FCSTD DOCUMENT  (FreeCAD 1.0R39319 (Git))
Label: FrontAssembly
License: All rights reserved
LicenseURL: https://en.wikipedia.org/wiki/All_rights_reserved
objects: App::FeaturePython×19, App::Link×17, Assembly::JointGroup×1, Assembly::AssemblyObject×1
EXTERNAL_REF file=../Parts/FrontCover.FCStd obj=Part
EXTERNAL_REF file=../Parts/WheelLinkage/WheelLinkageTopLeft.FCStd obj=Body
EXTERNAL_REF file=../Parts/WheelLinkage/WheelLinkageBottomLeft.FCStd obj=Part
EXTERNAL_REF file=../Parts/WheelLinkage/WheelLinkageTopRight.FCStd obj=Part
EXTERNAL_REF file=../Parts/WheelLinkage/WheelLinkageBottomRight.FCStd obj=Part
EXTERNAL_REF file=../Parts/FrontWheelAxle/FrontWheelAxleLeft.FCStd obj=Part
EXTERNAL_REF file=../Parts/FrontWheelAxle/FrontWheelAxleRight.FCStd obj=Part
EXTERNAL_REF file=../Parts/S0004m.FCStd obj=Part
EXTERNAL_REF file=../Parts/TBoneLinkage/TBoneLinkageTop.FCStd obj=Part
EXTERNAL_REF file=../Parts/TBoneLinkage/TBoneLinkageBottom.FCStd obj=Part
EXTERNAL_REF file=../Parts/TransferLinkage/TransferLinkageLeft.FCStd obj=Part
EXTERNAL_REF file=../Parts/TransferLinkage/TransferLinkageRight.FCStd obj=Part
EXTERNAL_REF file=../Parts/FrontWheelStopper.FCStd obj=Part
EXTERNAL_REF file=../Parts/Wheel.FCStd obj=Part
EXTERNAL_REF file=../Parts/RpiCamera.FCStd obj=rpiCameraMAssembly

FEATURE [App::Link] FrontCoverPart
  LinkedObject = -> <external ../Parts/FrontCover.FCStd>#Part
FEATURE [App::FeaturePython] GroundedJoint  # Assembly grounded joint (typed FeaturePython)
  ObjectToGround = -> FrontCoverPart
FEATURE [App::Link] WheelLinkageTopLeftBody
  LinkPlacement = pos=(-34,-2e-16,0) rot=(0,0,1;0.017527rad)
  LinkedObject = -> <external ../Parts/WheelLinkage/WheelLinkageTopLeft.FCStd>#Body
  Placement = pos=(-34,-2e-16,0) rot=(0,0,1;0.017527rad)
FEATURE [App::FeaturePython] Joint  label="Revolute"  # Assembly joint (typed FeaturePython)
  Activated = true
  AngleMax = 0
  AngleMin = 0
  Detach1 = false
  Detach2 = false
  Distance = 0
  Distance2 = 0
  EnableAngleMax = false
  EnableAngleMin = false
  EnableLengthMax = false
  EnableLengthMin = false
  JointType = 1 (Revolute)
  LengthMax = 0
  LengthMin = 0
  Placement2 = pos=(-34,-2e-16,0) rot=(0,0,1;0rad)
  Reference1 = -> Assembly [WheelLinkageTopLeftBody.Edge16,WheelLinkageTopLeftBody.Edge16]
  Reference2 = -> Assembly [FrontCoverPart.Body.Edge88,FrontCoverPart.Body.Edge88]
FEATURE [App::Link] WheelLinkageBottomLeftPart
  LinkPlacement = pos=(-34,-2e-16,-7) rot=(0,0,1;0.017527rad)
  LinkedObject = -> <external ../Parts/WheelLinkage/WheelLinkageBottomLeft.FCStd>#Part
  Placement = pos=(-34,-2e-16,-7) rot=(0,0,1;0.017527rad)
FEATURE [App::FeaturePython] Joint001  label="Fixed"  # Assembly joint (typed FeaturePython)
  Activated = true
  AngleMax = 0
  AngleMin = 0
  Detach1 = false
  Detach2 = false
  Distance = 0
  Distance2 = 0
  EnableAngleMax = false
  EnableAngleMin = false
  EnableLengthMax = false
  EnableLengthMin = false
  JointType = 0 (Fixed)
  LengthMax = 0
  LengthMin = 0
  Placement1 = pos=(-5,0,7) rot=(0,0,1;0rad)
  Placement2 = pos=(-5,0,0) rot=(1,0,0;3.14159rad)
  Reference1 = -> Assembly [WheelLinkageBottomLeftPart.Body.Edge27,WheelLinkageBottomLeftPart.Body.Edge27]
  Reference2 = -> Assembly [WheelLinkageTopLeftBody.Edge15,WheelLinkageTopLeftBody.Edge15]
FEATURE [App::Link] WheelLinkageTopRightPart
  LinkPlacement = pos=(34,0,0) rot=(0,0,1;0.017627rad)
  LinkedObject = -> <external ../Parts/WheelLinkage/WheelLinkageTopRight.FCStd>#Part
  Placement = pos=(34,0,0) rot=(0,0,1;0.017627rad)
FEATURE [App::FeaturePython] Joint002  label="Revolute001"  # Assembly joint (typed FeaturePython)
  Activated = true
  AngleMax = 0
  AngleMin = 0
  Detach1 = false
  Detach2 = false
  Distance = 0
  Distance2 = 0
  EnableAngleMax = false
  EnableAngleMin = false
  EnableLengthMax = false
  EnableLengthMin = false
  JointType = 1 (Revolute)
  LengthMax = 0
  LengthMin = 0
  Placement1 = pos=(0,0,0) rot=(0,1,0;3.14159rad)
  Placement2 = pos=(34,0,0) rot=(0,0,1;0rad)
  Reference1 = -> Assembly [WheelLinkageTopRightPart.Part__Mirroring.Edge16,WheelLinkageTopRightPart.Part__Mirroring.Edge16]
  Reference2 = -> Assembly [FrontCoverPart.Body.Edge94,FrontCoverPart.Body.Edge94]
FEATURE [App::Link] WheelLinkageBottomRightPart
  LinkPlacement = pos=(34,0,-7) rot=(0,0,1;0.017627rad)
  LinkedObject = -> <external ../Parts/WheelLinkage/WheelLinkageBottomRight.FCStd>#Part
  Placement = pos=(34,0,-7) rot=(0,0,1;0.017627rad)
FEATURE [App::FeaturePython] Joint003  label="Fixed001"  # Assembly joint (typed FeaturePython)
  Activated = true
  AngleMax = 0
  AngleMin = 0
  Detach1 = false
  Detach2 = false
  Distance = 0
  Distance2 = 0
  EnableAngleMax = false
  EnableAngleMin = false
  EnableLengthMax = false
  EnableLengthMin = false
  JointType = 0 (Fixed)
  LengthMax = 0
  LengthMin = 0
  Placement1 = pos=(5,0,7) rot=(0,1,0;3.14159rad)
  Placement2 = pos=(5,0,0) rot=(0,0,1;3.14159rad)
  Reference1 = -> Assembly [WheelLinkageBottomRightPart.Part__Mirroring.Edge27,WheelLinkageBottomRightPart.Part__Mirroring.Edge27]
  Reference2 = -> Assembly [WheelLinkageTopRightPart.Part__Mirroring.Edge15,WheelLinkageTopRightPart.Part__Mirroring.Edge15]
FEATURE [App::Link] FrontWheelAxleLeftPart
  LinkPlacement = pos=(-31.0005,0.0525794,-3.5) rot=(0,0,1;0.017527rad)
  LinkedObject = -> <external ../Parts/FrontWheelAxle/FrontWheelAxleLeft.FCStd>#Part
  Placement = pos=(-31.0005,0.0525794,-3.5) rot=(0,0,1;0.017527rad)
FEATURE [App::FeaturePython] Joint004  label="Fixed002"  # Assembly joint (typed FeaturePython)
  Activated = true
  AngleMax = 0
  AngleMin = 0
  Detach1 = false
  Detach2 = false
  Distance = 0
  Distance2 = 0
  EnableAngleMax = false
  EnableAngleMin = false
  EnableLengthMax = false
  EnableLengthMin = false
  JointType = 0 (Fixed)
  LengthMax = 0
  LengthMin = 0
  Offset2 = pos=(0,0,0) rot=(0,0,-1;1.5708rad)
  Placement1 = pos=(-3,-2e-16,1.5) rot=(0,0,-1;1.5708rad)
  Placement2 = pos=(0,0,-2) rot=(0,0,-1;1.5708rad)
  Reference1 = -> Assembly [FrontWheelAxleLeftPart.Body.Edge27,FrontWheelAxleLeftPart.Body.Edge27]
  Reference2 = -> Assembly [WheelLinkageTopLeftBody.Edge22,WheelLinkageTopLeftBody.Edge22]
FEATURE [App::Link] FrontWheelAxleRightPart
  LinkPlacement = pos=(31.0005,-0.0528788,-3.5) rot=(0,0,1;0.017627rad)
  LinkedObject = -> <external ../Parts/FrontWheelAxle/FrontWheelAxleRight.FCStd>#Part
  Placement = pos=(31.0005,-0.0528788,-3.5) rot=(0,0,1;0.017627rad)
FEATURE [App::FeaturePython] Joint005  label="Fixed003"  # Assembly joint (typed FeaturePython)
  Activated = true
  AngleMax = 0
  AngleMin = 0
  Detach1 = false
  Detach2 = false
  Distance = 0
  Distance2 = 0
  EnableAngleMax = false
  EnableAngleMin = false
  EnableLengthMax = false
  EnableLengthMin = false
  JointType = 0 (Fixed)
  LengthMax = 0
  LengthMin = 0
  Offset2 = pos=(0,0,0) rot=(0,0,-1;1.5708rad)
  Placement1 = pos=(3,-2e-16,1.5) rot=(-0.707107,0.707107,0;3.14159rad)
  Placement2 = pos=(0,0,-2) rot=(-0.707107,0.707107,0;3.14159rad)
  Reference1 = -> Assembly [FrontWheelAxleRightPart.Part__Mirroring.Edge27,FrontWheelAxleRightPart.Part__Mirroring.Edge27]
  Reference2 = -> Assembly [WheelLinkageTopRightPart.Part__Mirroring.Edge22,WheelLinkageTopRightPart.Part__Mirroring.Edge22]
FEATURE [App::Link] S0004mPart
  LinkPlacement = pos=(0,-9.55,24.5) rot=(1,0,0;3.14159rad)
  LinkedObject = -> <external ../Parts/S0004m.FCStd>#Part
  Placement = pos=(0,-9.55,24.5) rot=(1,0,0;3.14159rad)
FEATURE [App::Link] TBoneLinkageTopPart
  LinkPlacement = pos=(0,-4,1e-16) rot=(0,0,1;0.016716rad)
  LinkedObject = -> <external ../Parts/TBoneLinkage/TBoneLinkageTop.FCStd>#Part
  Placement = pos=(0,-4,1e-16) rot=(0,0,1;0.016716rad)
FEATURE [App::Link] TBoneLinkageBottomPart
  LinkPlacement = pos=(2e-16,-4,-7) rot=(0,0,1;0.016716rad)
  LinkedObject = -> <external ../Parts/TBoneLinkage/TBoneLinkageBottom.FCStd>#Part
  Placement = pos=(2e-16,-4,-7) rot=(0,0,1;0.016716rad)
FEATURE [App::FeaturePython] Joint007  label="Revolute002"  # Assembly joint (typed FeaturePython)
  Activated = true
  AngleMax = 0
  AngleMin = 0
  Detach1 = false
  Detach2 = false
  Distance = 0
  Distance2 = 0
  EnableAngleMax = false
  EnableAngleMin = false
  EnableLengthMax = false
  EnableLengthMin = false
  JointType = 1 (Revolute)
  LengthMax = 0
  LengthMin = 0
  Placement1 = pos=(0,0,-2) rot=(0,0,1;0rad)
  Placement2 = pos=(0,-5.55,26.5) rot=(0,0,1;0rad)
  Reference1 = -> Assembly [TBoneLinkageTopPart.Body.Edge22,TBoneLinkageTopPart.Body.Edge22]
  Reference2 = -> Assembly [S0004mPart.Body.Edge51,S0004mPart.Body.Edge51]
FEATURE [App::FeaturePython] Joint008  label="Fixed005"  # Assembly joint (typed FeaturePython)
  Activated = true
  AngleMax = 0
  AngleMin = 0
  Detach1 = false
  Detach2 = false
  Distance = 0
  Distance2 = 0
  EnableAngleMax = false
  EnableAngleMin = false
  EnableLengthMax = false
  EnableLengthMin = false
  JointType = 0 (Fixed)
  LengthMax = 0
  LengthMin = 0
  Placement1 = pos=(-5,-12,7) rot=(0,0,1;0rad)
  Placement2 = pos=(-5,-12,0) rot=(0,0,1;0rad)
  Reference1 = -> Assembly [TBoneLinkageBottomPart.Body.Edge43,TBoneLinkageBottomPart.Body.Edge43]
  Reference2 = -> Assembly [TBoneLinkageTopPart.Body.Edge16,TBoneLinkageTopPart.Body.Edge16]
FEATURE [App::Link] TransferLinkageLeftPart
  LinkPlacement = pos=(-4.79872,-16.0819,-4.5) rot=(0,0,-1;0.136224rad)
  LinkedObject = -> <external ../Parts/TransferLinkage/TransferLinkageLeft.FCStd>#Part
  Placement = pos=(-4.79872,-16.0819,-4.5) rot=(0,0,-1;0.136224rad)
FEATURE [App::Link] TransferLinkageRightPart
  LinkPlacement = pos=(5.19989,-15.9147,-4.5) rot=(0,0,1;0.133954rad)
  LinkedObject = -> <external ../Parts/TransferLinkage/TransferLinkageRight.FCStd>#Part
  Placement = pos=(5.19989,-15.9147,-4.5) rot=(0,0,1;0.133954rad)
FEATURE [App::FeaturePython] Joint009  label="Revolute003"  # Assembly joint (typed FeaturePython)
  Activated = true
  AngleMax = 0
  AngleMin = 0
  Detach1 = false
  Detach2 = false
  Distance = 0
  Distance2 = 0
  EnableAngleMax = false
  EnableAngleMin = false
  EnableLengthMax = false
  EnableLengthMin = false
  JointType = 1 (Revolute)
  LengthMax = 0
  LengthMin = 0
  Placement1 = pos=(0,0,2) rot=(0,0,1;0rad)
  Placement2 = pos=(-5,-12,-2.5) rot=(1,0,0;3.14159rad)
  Reference1 = -> Assembly [TransferLinkageLeftPart.Body.Edge24,TransferLinkageLeftPart.Body.Edge24]
  Reference2 = -> Assembly [TBoneLinkageTopPart.Body.Edge30,TBoneLinkageTopPart.Body.Edge30]
FEATURE [App::FeaturePython] Joint010  label="Cylindrical"  # Assembly joint (typed FeaturePython)
  Activated = true
  AngleMax = 0
  AngleMin = 0
  Detach1 = false
  Detach2 = false
  Distance = 0
  Distance2 = 0
  EnableAngleMax = false
  EnableAngleMin = false
  EnableLengthMax = false
  EnableLengthMin = false
  JointType = 2 (Cylindrical)
  LengthMax = 0
  LengthMin = 0
  Placement1 = pos=(-32,0,2) rot=(0,0,1;0rad)
  Placement2 = pos=(-2.70757,-11.6906,-2.5) rot=(1,0,0;3.14159rad)
  Reference1 = -> Assembly [TransferLinkageLeftPart.Body.Edge27,TransferLinkageLeftPart.Body.Edge27]
  Reference2 = -> Assembly [WheelLinkageTopLeftBody.Edge26,WheelLinkageTopLeftBody.Edge26]
FEATURE [App::FeaturePython] Joint011  label="Revolute004"  # Assembly joint (typed FeaturePython)
  Activated = true
  AngleMax = 0
  AngleMin = 0
  Detach1 = false
  Detach2 = false
  Distance = 0
  Distance2 = 0
  EnableAngleMax = false
  EnableAngleMin = false
  EnableLengthMax = false
  EnableLengthMin = false
  JointType = 1 (Revolute)
  LengthMax = 0
  LengthMin = 0
  Placement1 = pos=(0,0,2) rot=(0,1,0;3.14159rad)
  Placement2 = pos=(5,-12,-2.5) rot=(1,0,0;3.14159rad)
  Reference1 = -> Assembly [TransferLinkageRightPart.Part__Mirroring.Edge24,TransferLinkageRightPart.Part__Mirroring.Edge24]
  Reference2 = -> Assembly [TBoneLinkageTopPart.Body.Edge31,TBoneLinkageTopPart.Body.Edge31]
FEATURE [App::FeaturePython] Joint012  label="Cylindrical001"  # Assembly joint (typed FeaturePython)
  Activated = true
  AngleMax = 0
  AngleMin = 0
  Detach1 = false
  Detach2 = false
  Distance = 0
  Distance2 = 0
  EnableAngleMax = false
  EnableAngleMin = false
  EnableLengthMax = false
  EnableLengthMin = false
  JointType = 2 (Cylindrical)
  LengthMax = 0
  LengthMin = 0
  Placement1 = pos=(32,0,2) rot=(0,1,0;3.14159rad)
  Placement2 = pos=(2.70757,-11.6906,-2.5) rot=(0,0,1;3.14159rad)
  Reference1 = -> Assembly [TransferLinkageRightPart.Part__Mirroring.Edge27,TransferLinkageRightPart.Part__Mirroring.Edge27]
  Reference2 = -> Assembly [WheelLinkageTopRightPart.Part__Mirroring.Edge26,WheelLinkageTopRightPart.Part__Mirroring.Edge26]
FEATURE [App::Link] FrontWheelStopperPart
  LinkPlacement = pos=(-42.9986,-0.157738,-3.5) rot=(0,0,1;0.017527rad)
  LinkedObject = -> <external ../Parts/FrontWheelStopper.FCStd>#Part
  Placement = pos=(-42.9986,-0.157738,-3.5) rot=(0,0,1;0.017527rad)
FEATURE [App::Link] FrontWheelStopperPart001
  LinkPlacement = pos=(42.9986,0.158636,-3.5) rot=(0,0,1;3.15922rad)
  LinkedObject = -> <external ../Parts/FrontWheelStopper.FCStd>#Part
  Placement = pos=(42.9986,0.158636,-3.5) rot=(0,0,1;3.15922rad)
FEATURE [App::FeaturePython] Joint013  label="Fixed006"  # Assembly joint (typed FeaturePython)
  Activated = true
  AngleMax = 0
  AngleMin = 0
  Detach1 = false
  Detach2 = false
  Distance = 0
  Distance2 = 0
  EnableAngleMax = false
  EnableAngleMin = false
  EnableLengthMax = false
  EnableLengthMin = false
  JointType = 0 (Fixed)
  LengthMax = 0
  LengthMin = 0
  Placement1 = pos=(-2,-2e-16,1.8e-15) rot=(0.57735,0.57735,0.57735;2.0944rad)
  Placement2 = pos=(-14,3e-15,7.1e-15) rot=(0.57735,0.57735,-0.57735;4.18879rad)
  Reference1 = -> Assembly [FrontWheelStopperPart.Body.Edge22,FrontWheelStopperPart.Body.Edge22]
  Reference2 = -> Assembly [FrontWheelAxleLeftPart.Body.Edge20,FrontWheelAxleLeftPart.Body.Edge20]
FEATURE [App::Link] WheelPart
  LinkPlacement = pos=(-35.9997,-0.035053,-3.5) rot=(0,0,1;0.017527rad)
  LinkedObject = -> <external ../Parts/Wheel.FCStd>#Part
  Placement = pos=(-35.9997,-0.035053,-3.5) rot=(0,0,1;0.017527rad)
FEATURE [App::Link] WheelPart001
  LinkPlacement = pos=(35.9997,0.0352525,-3.5) rot=(0,0,1;3.15922rad)
  LinkedObject = -> <external ../Parts/Wheel.FCStd>#Part
  Placement = pos=(35.9997,0.0352525,-3.5) rot=(0,0,1;3.15922rad)
FEATURE [App::FeaturePython] Joint014  label="Fixed007"  # Assembly joint (typed FeaturePython)
  Activated = true
  AngleMax = 0
  AngleMin = 0
  Detach1 = false
  Detach2 = false
  Distance = 0
  Distance2 = 0
  EnableAngleMax = false
  EnableAngleMin = false
  EnableLengthMax = false
  EnableLengthMin = false
  JointType = 0 (Fixed)
  LengthMax = 0
  LengthMin = 0
  Offset2 = pos=(0,0,0) rot=(0,0,1;3.14159rad)
  Placement1 = pos=(-2,-2e-16,1.8e-15) rot=(0.57735,0.57735,0.57735;2.0944rad)
  Placement2 = pos=(14,8.7e-15,3e-16) rot=(-0.57735,0.57735,0.57735;4.18879rad)
  Reference1 = -> Assembly [FrontWheelStopperPart001.Body.Edge22,FrontWheelStopperPart001.Body.Edge22]
  Reference2 = -> Assembly [FrontWheelAxleRightPart.Part__Mirroring.Edge6,FrontWheelAxleRightPart.Part__Mirroring.Edge6]
FEATURE [App::FeaturePython] Joint015  label="Fixed008"  # Assembly joint (typed FeaturePython)
  Activated = true
  AngleMax = 0
  AngleMin = 0
  Detach1 = false
  Detach2 = false
  Distance = 0
  Distance2 = 0
  EnableAngleMax = false
  EnableAngleMin = false
  EnableLengthMax = false
  EnableLengthMin = false
  JointType = 0 (Fixed)
  LengthMax = 0
  LengthMin = 0
  Placement1 = pos=(-11,7.8e-15,-3.9e-15) rot=(0.57735,0.57735,0.57735;2.0944rad)
  Placement2 = pos=(-16,4e-15,7.1e-15) rot=(0.57735,0.57735,-0.57735;4.18879rad)
  Reference1 = -> Assembly [WheelPart.Body.Edge25,WheelPart.Body.Edge25]
  Reference2 = -> Assembly [FrontWheelAxleLeftPart.Body.Edge33,FrontWheelAxleLeftPart.Body.Edge33]
FEATURE [App::FeaturePython] Joint016  label="Fixed009"  # Assembly joint (typed FeaturePython)
  Activated = true
  AngleMax = 0
  AngleMin = 0
  Detach1 = false
  Detach2 = false
  Distance = 0
  Distance2 = 0
  EnableAngleMax = false
  EnableAngleMin = false
  EnableLengthMax = false
  EnableLengthMin = false
  JointType = 0 (Fixed)
  LengthMax = 0
  LengthMin = 0
  Offset2 = pos=(0,0,0) rot=(0,0,1;3.14159rad)
  Placement1 = pos=(-11,7.8e-15,-3.9e-15) rot=(0.57735,0.57735,0.57735;2.0944rad)
  Placement2 = pos=(16,4e-15,7.1e-15) rot=(-0.57735,0.57735,0.57735;4.18879rad)
  Reference1 = -> Assembly [WheelPart001.Body.Edge25,WheelPart001.Body.Edge25]
  Reference2 = -> Assembly [FrontWheelAxleRightPart.Part__Mirroring.Edge33,FrontWheelAxleRightPart.Part__Mirroring.Edge33]
FEATURE [App::Link] RpiCameraPart
  LinkPlacement = pos=(-3.5e-15,11.25,15.75) rot=(0,0,1;0rad)
  LinkedObject = -> <external ../Parts/RpiCamera.FCStd>#rpiCameraMAssembly
  Placement = pos=(-3.5e-15,11.25,15.75) rot=(0,0,1;0rad)
FEATURE [App::FeaturePython] Joint017  label="Fixed010"  # Assembly joint (typed FeaturePython)
  Activated = true
  AngleMax = 0
  AngleMin = 0
  Detach1 = false
  Detach2 = false
  Distance = 0
  Distance2 = 0
  EnableAngleMax = false
  EnableAngleMin = false
  EnableLengthMax = false
  EnableLengthMin = false
  JointType = 0 (Fixed)
  LengthMax = 0
  LengthMin = 0
  Offset2 = pos=(0,0,1.7) rot=(0,0,-1;1.5708rad)
  Placement1 = pos=(10.25,0.1,3.75) rot=(-0.57735,0.57735,0.57735;2.0944rad)
  Placement2 = pos=(10.25,11.35,19.5) rot=(-0.57735,0.57735,0.57735;2.0944rad)
  Reference1 = -> Assembly [RpiCameraPart.Part__Feature.Edge767,RpiCameraPart.Part__Feature.Edge767]
  Reference2 = -> Assembly [FrontCoverPart.Body.Edge102,FrontCoverPart.Body.Edge102]
FEATURE [App::FeaturePython] Joint018  label="Fixed011"  # Assembly joint (typed FeaturePython)
  Activated = true
  AngleMax = 0
  AngleMin = 0
  Detach1 = false
  Detach2 = false
  Distance = 0
  Distance2 = 0
  EnableAngleMax = false
  EnableAngleMin = false
  EnableLengthMax = false
  EnableLengthMin = false
  JointType = 0 (Fixed)
  LengthMax = 0
  LengthMin = 0
  Placement1 = pos=(0,-21.35,8.5) rot=(0,0,1;0rad)
  Placement2 = pos=(0,11.8,16) rot=(0,0,1;0rad)
  Reference1 = -> Assembly [FrontCoverPart.Body.Edge133,FrontCoverPart.Body.Edge133]
  Reference2 = -> Assembly [S0004mPart.Body.Edge42,S0004mPart.Body.Edge42]
FEATURE [Assembly::JointGroup] Joints
  Group = -> [GroundedJoint,Joint,Joint001,Joint002,Joint003,Joint004,Joint005,Joint007,Joint008,Joint009,Joint010,Joint011,Joint012,Joint013,Joint014,Joint015,Joint016,Joint017,Joint018]
FEATURE [Assembly::AssemblyObject] Assembly  label="FrontAssembly"
  Group = -> [Joints,FrontCoverPart,GroundedJoint,WheelLinkageTopLeftBody,Joint,WheelLinkageBottomLeftPart,Joint001,WheelLinkageTopRightPart,Joint002,WheelLinkageBottomRightPart,Joint003,FrontWheelAxleLeftPart,Joint004,FrontWheelAxleRightPart,Joint005,S0004mPart,TBoneLinkageTopPart,TBoneLinkageBottomPart,Joint007,Joint008,TransferLinkageLeftPart,TransferLinkageRightPart,Joint009,Joint010,Joint011,Joint012,+11 more]
  Origin = -> Origin
  Type = Assembly

RESOLVED EXTERNAL PARTS (link-assembly join: the EXTERNAL_REF files above that resolve inside this repo's crawl, each included once):
---- part ../Parts/FrontCover.FCStd = doc fcstd_34d13ded4ae3 ----
FCSTD DOCUMENT  (FreeCAD 1.0R39319 (Git))
Label: FrontCover
License: All rights reserved
LicenseURL: https://en.wikipedia.org/wiki/All_rights_reserved
objects: Sketcher::SketchObject×5, PartDesign::Pad×3, PartDesign::SubShapeBinder×2, PartDesign::Pocket×2, PartDesign::Chamfer×1, PartDesign::Body×1, App::Part×1
note: 31 computed .brp shape members not serialized (recipe doc carries the construction recipe); baked Part::Feature solids carry a one-line shape summary decoded from their .brp
EXTERNAL_REF file=../Models/SteeringAckermannModel.FCStd obj=Part
EXTERNAL_REF file=Chassis.FCStd obj=Part

FEATURE [PartDesign::SubShapeBinder] Binder  label="SteeringAckermannModel"
  BindCopyOnChange = 0
  BindMode = 0
  ClaimChildren = false
  Context = -> Part [Body.Binder.]
  Fuse = false
  MakeFace = true
  OffsetFill = false
  OffsetIntersection = false
  OffsetJoinType = 0
  OffsetOpenResult = false
  PartialLoad = false
  Refine = true
  Relative = true
  Support = -> [<external ../Models/SteeringAckermannModel.FCStd>#Part[Sketch001.]]
  _Version = 2
FEATURE [PartDesign::SubShapeBinder] Binder001  label="ChassisSketch002"
  BindCopyOnChange = 0
  BindMode = 0
  ClaimChildren = false
  Context = -> Part [Body.Binder001.]
  Fuse = false
  MakeFace = true
  OffsetFill = false
  OffsetIntersection = false
  OffsetJoinType = 0
  OffsetOpenResult = false
  PartialLoad = false
  Refine = true
  Relative = true
  Support = -> [<external Chassis.FCStd>#Part[Body.Sketch002.]]
  _Version = 2
FEATURE [Sketcher::SketchObject] Sketch
  ArcFitTolerance = 1e-06
  AttachmentSupport = -> [XY_Plane001]
  ExternalGeometry = -> [Binder001,Binder]
  FullyConstrained = true
  MakeInternals = false
  MapMode = 5
  sketch-geometry (27):
    g0: LineSegment StartX=-11.3 StartY=-4 StartZ=0 EndX=-26 EndY=-4 EndZ=0
    g1: LineSegment StartX=-26 StartY=-4 StartZ=0 EndX=-34 EndY=-4 EndZ=0
    g2: LineSegment StartX=-34 StartY=4 StartZ=0 EndX=-26 EndY=4 EndZ=0
    g3: LineSegment StartX=-26 StartY=4 StartZ=0 EndX=-10 EndY=22 EndZ=0
    g4: ArcOfCircle CenterX=-34 CenterY=-2e-16 CenterZ=0 NormalX=0 NormalY=0 NormalZ=1 AngleXU=0 Radius=4 StartAngle=1.5708 EndAngle=4.71239
    g5: LineSegment StartX=11.3 StartY=-4 StartZ=0 EndX=26 EndY=-4 EndZ=0
    g6: LineSegment StartX=26 StartY=4 StartZ=0 EndX=10 EndY=22 EndZ=0
    g7: LineSegment StartX=26 StartY=-4 StartZ=0 EndX=34 EndY=-4 EndZ=0
    g8: LineSegment StartX=26 StartY=4 StartZ=0 EndX=34 EndY=4 EndZ=0
    g9: ArcOfCircle CenterX=34 CenterY=0 CenterZ=0 NormalX=0 NormalY=0 NormalZ=1 AngleXU=0 Radius=4 StartAngle=4.71239 EndAngle=7.85398
    g10: LineSegment StartX=-10 StartY=22 StartZ=0 EndX=10 EndY=22 EndZ=0
    g11: LineSegment StartX=-11.3 StartY=-4 StartZ=0 EndX=-6 EndY=-23.75 EndZ=0
    g12: LineSegment StartX=-6 StartY=-23.75 StartZ=0 EndX=6 EndY=-23.75 EndZ=0
    g13: LineSegment StartX=6 StartY=-23.75 StartZ=0 EndX=11.3 EndY=-4 EndZ=0
    g14: LineSegment StartX=-4.35 StartY=0.65 StartZ=0 EndX=-4.35 EndY=-19.75 EndZ=0
    g15: LineSegment StartX=-4.35 StartY=-19.75 StartZ=0 EndX=4.35 EndY=-19.75 EndZ=0
    g16: LineSegment StartX=4.35 StartY=-19.75 StartZ=0 EndX=4.35 EndY=0.65 EndZ=0
    g17: LineSegment StartX=4.35 StartY=0.65 StartZ=0 EndX=-4.35 EndY=0.65 EndZ=0
    g18: GeomPoint X=4e-16 Y=-9.55 Z=0
    g19: Circle CenterX=0 CenterY=2.25 CenterZ=0 NormalX=0 NormalY=0 NormalZ=1 AngleXU=0 Radius=0.86
    g20: Circle CenterX=-7.473e-13 CenterY=-21.35 CenterZ=0 NormalX=0 NormalY=0 NormalZ=1 AngleXU=0 Radius=0.86
    g21: Circle CenterX=-34 CenterY=-2e-16 CenterZ=0 NormalX=0 NormalY=0 NormalZ=1 AngleXU=0 Radius=1.5
    g22: Circle CenterX=34 CenterY=0 CenterZ=0 NormalX=0 NormalY=0 NormalZ=1 AngleXU=0 Radius=1.5
    g23: Circle CenterX=-22 CenterY=0 CenterZ=0 NormalX=0 NormalY=0 NormalZ=1 AngleXU=0 Radius=1.65
    g24: Circle CenterX=-11.3195 CenterY=16 CenterZ=0 NormalX=0 NormalY=0 NormalZ=1 AngleXU=0 Radius=1.65
    g25: Circle CenterX=11.3195 CenterY=16 CenterZ=0 NormalX=0 NormalY=0 NormalZ=1 AngleXU=0 Radius=1.65
    g26: Circle CenterX=22 CenterY=0 CenterZ=0 NormalX=0 NormalY=0 NormalZ=1 AngleXU=0 Radius=1.65
  constraints (58):
    c: Coincident(g0,g-3)
    c: Coincident(g0,g-4)
    c: Coincident(g1,g0)
    c: Coincident(g2,g-7)
    c: Coincident(g3,g2)
    c: Coincident(g3,g-8)
    c: Tangent(g1,g4) = 1.5708
    c: Tangent(g2,g4) = 1.5708
    c: Coincident(g1,g-5)
    c: Horizontal(g2)
    c: Coincident(g5,g-12)
    c: Coincident(g5,g-13)
    c: Coincident(g6,g-16)
    c: Coincident(g6,g-17)
    c: Coincident(g7,g5)
    c: Coincident(g8,g6)
    c: Tangent(g7,g9) = -1.5708
    c: Tangent(g9,g8) = 1.5708
    c: Horizontal(g8)
    c: Coincident(g7,g-14)
    c: Coincident(g10,g3)
    c: Coincident(g10,g6)
    c: Coincident(g11,g0)
    c: Coincident(g12,g11)
    c: Coincident(g13,g12)
    c: Coincident(g13,g5)
    c: Symmetric(g11,g12,g-2)
    c: DistanceX(g12,g12) = 12
    c: Coincident(g14,g15)
    c: Coincident(g15,g16)
    c: Coincident(g16,g17)
    c: Coincident(g17,g14)
    c: Vertical(g14)
    c: Vertical(g16)
    c: Horizontal(g17)
    c: Symmetric(g14,g15,g-2)
    c: DistanceX(g15,g15) = 8.7
    c: DistanceY(g14,g14) = 20.4
    c: Distance(g-21,g17) = 4.65
    c: Distance(g12,g15) = 4
    c: Symmetric(g14,g16,g18)
    c: Diameter(g19) = 1.72
    c: PointOnObject(g19,g-2)
    c: Equal(g19,g20)
    c: Symmetric(g19,g20,g18)
    c: Distance(g19,g17) = 1.6
    c: Coincident(g21,g4)
    c: Equal(g21,g-9)
    c: Coincident(g22,g9)
    c: Equal(g22,g-18)
    c: Coincident(g23,g-10)
    c: Coincident(g24,g-11)
    c: Coincident(g25,g-20)
    c: Coincident(g26,g-19)
    c: Equal(g23,g26)
    c: Equal(g24,g25)
    c: Diameter(g23) = 3.3
    c: Diameter(g24) = 3.3
FEATURE [PartDesign::Pad] Pad
  Direction = (0,0,1)
  Length = 3
  Length2 = 10
  Profile = -> Sketch
  ReferenceAxis = -> Sketch [N_Axis]
  Refine = true
  Suppressed = false
  Type = 0
FEATURE [Sketcher::SketchObject] Sketch001
  ArcFitTolerance = 1e-06
  AttachmentSupport = -> [Pad]
  ExternalGeometry = -> [Sketch]
  FullyConstrained = true
  MakeInternals = false
  MapMode = 5
  Placement = pos=(0,0,3) rot=(0,0,1;0rad)
  sketch-geometry (13):
    g0: LineSegment StartX=-4.35 StartY=-19.75 StartZ=0 EndX=4.35 EndY=-19.75 EndZ=0
    g1: LineSegment StartX=4.35 StartY=-19.75 StartZ=0 EndX=4.35 EndY=0.65 EndZ=0
    g2: LineSegment StartX=4.35 StartY=0.65 StartZ=0 EndX=-4.35 EndY=0.65 EndZ=0
    g3: LineSegment StartX=-4.35 StartY=0.65 StartZ=0 EndX=-4.35 EndY=-19.75 EndZ=0
    g4: Circle CenterX=0 CenterY=-21.35 CenterZ=0 NormalX=0 NormalY=0 NormalZ=1 AngleXU=0 Radius=0.86
    g5: Circle CenterX=0 CenterY=2.25 CenterZ=0 NormalX=0 NormalY=0 NormalZ=1 AngleXU=0 Radius=0.86
    g6: LineSegment StartX=-6 StartY=-23.75 StartZ=0 EndX=6 EndY=-23.75 EndZ=0
    g7: LineSegment [constr] StartX=-9.81063 StartY=-9.55 StartZ=0 EndX=9.81063 EndY=-9.55 EndZ=0
    g8: LineSegment StartX=-6 StartY=-23.75 StartZ=0 EndX=-9.81063 EndY=-9.55 EndZ=0
    g9: LineSegment StartX=6 StartY=-23.75 StartZ=0 EndX=9.81063 EndY=-9.55 EndZ=0
    g10: LineSegment StartX=-6 StartY=4.65 StartZ=0 EndX=-9.81063 EndY=-9.55 EndZ=0
    g11: LineSegment StartX=-6 StartY=4.65 StartZ=0 EndX=6 EndY=4.65 EndZ=0
    g12: LineSegment StartX=6 StartY=4.65 StartZ=0 EndX=9.81063 EndY=-9.55 EndZ=0
  constraints (27):
    c: Coincident(g0,g-10)
    c: Coincident(g0,g-11)
    c: Coincident(g1,g0)
    c: Coincident(g1,g-12)
    c: Coincident(g2,g1)
    c: Coincident(g2,g-12)
    c: Coincident(g3,g2)
    c: Coincident(g3,g0)
    c: Coincident(g4,g-7)
    c: Equal(g4,g-7)
    c: Coincident(g5,g-8)
    c: Equal(g5,g-8)
    c: Coincident(g6,g-5)
    c: Coincident(g6,g-6)
    c: Horizontal(g7)
    c: Symmetric(g7,g7,g-3)
    c: PointOnObject(g7,g-4)
    c: Coincident(g8,g6)
    c: Coincident(g8,g7)
    c: Coincident(g9,g6)
    c: Coincident(g9,g7)
    c: Coincident(g10,g11)
    c: Coincident(g12,g11)
    c: Symmetric(g6,g10,g7)
    c: Symmetric(g6,g11,g7)
    c: Coincident(g10,g7)
    c: Coincident(g12,g7)
FEATURE [PartDesign::Pad] Pad001
  BaseFeature = -> Pad
  Direction = (0,0,1)
  Length = 5.5
  Length2 = 10
  Profile = -> Sketch001
  ReferenceAxis = -> Sketch001 [N_Axis]
  Refine = true
  Suppressed = false
  Type = 0
FEATURE [Sketcher::SketchObject] Sketch002
  ArcFitTolerance = 1e-06
  AttachmentSupport = -> [Pad001]
  ExternalGeometry = -> [Sketch001]
  FullyConstrained = true
  MakeInternals = false
  MapMode = 5
  Placement = pos=(0,0,3) rot=(0,0,1;0rad)
  sketch-geometry (8):
    g0: LineSegment StartX=-12 StartY=6.65 StartZ=0 EndX=-12 EndY=-1.35 EndZ=0
    g1: LineSegment StartX=-12 StartY=-1.35 StartZ=0 EndX=-13.5 EndY=-1.35 EndZ=0
    g2: LineSegment StartX=-13.5 StartY=-1.35 StartZ=0 EndX=-13.5 EndY=9.65 EndZ=0
    g3: LineSegment StartX=-12 StartY=6.65 StartZ=0 EndX=12 EndY=6.65 EndZ=0
    g4: LineSegment StartX=-13.5 StartY=9.65 StartZ=0 EndX=13.5 EndY=9.65 EndZ=0
    g5: LineSegment StartX=12 StartY=6.65 StartZ=0 EndX=12 EndY=-1.35 EndZ=0
    g6: LineSegment StartX=12 StartY=-1.35 StartZ=0 EndX=13.5 EndY=-1.35 EndZ=0
    g7: LineSegment StartX=13.5 StartY=-1.35 StartZ=0 EndX=13.5 EndY=9.65 EndZ=0
  constraints (20):
    c: Vertical(g0)
    c: Coincident(g1,g0)
    c: Horizontal(g1)
    c: Coincident(g2,g1)
    c: Vertical(g2)
    c: Coincident(g3,g0)
    c: Coincident(g4,g2)
    c: Symmetric(g2,g4,g-2)
    c: Symmetric(g0,g3,g-2)
    c: Coincident(g5,g3)
    c: Coincident(g6,g5)
    c: Coincident(g7,g6)
    c: Coincident(g7,g4)
    c: Symmetric(g1,g6,g-2)
    c: Symmetric(g0,g5,g-2)
    c: DistanceX(g1,g1) = 1.5
    c: DistanceY(g0,g0) = 8
    c: Distance(g4,g3) = 3
    c: Distance(g-3,g3) = 2
    c: DistanceX(g4,g4) = 27
FEATURE [PartDesign::Pad] Pad002
  BaseFeature = -> Pad001
  Direction = (0,0,1)
  Length = 36
  Length2 = 10
  Profile = -> Sketch002
  ReferenceAxis = -> Sketch002 [N_Axis]
  Refine = true
  Suppressed = false
  Type = 0
FEATURE [PartDesign::Chamfer] Chamfer
  Angle = 15
  Base = -> Pad002 [Edge107,Edge99]
  BaseFeature = -> Pad002
  ChamferType = 2
  FlipDirection = false
  Refine = true
  Size = 29.85
  Size2 = 1
  SupportTransform = false
  Suppressed = false
  UseAllEdges = false
FEATURE [Sketcher::SketchObject] Sketch003
  ArcFitTolerance = 1e-06
  AttachmentSupport = -> [Chamfer]
  ExternalGeometry = -> [Chamfer]
  FullyConstrained = true
  MakeInternals = false
  MapMode = 5
  Placement = pos=(0,9.65,0) rot=(0,0.707107,0.707107;3.14159rad)
  sketch-geometry (14):
    g0: LineSegment [constr] StartX=-10.25 StartY=6 StartZ=0 EndX=10.25 EndY=6 EndZ=0
    g1: LineSegment [constr] StartX=10.25 StartY=6 StartZ=0 EndX=10.25 EndY=19.5 EndZ=0
    g2: LineSegment [constr] StartX=10.25 StartY=19.5 StartZ=0 EndX=-10.25 EndY=19.5 EndZ=0
    g3: LineSegment [constr] StartX=-10.25 StartY=19.5 StartZ=0 EndX=-10.25 EndY=6 EndZ=0
    g4: GeomPoint [constr] X=0 Y=12.75 Z=0
    g5: Circle CenterX=-10.25 CenterY=6 CenterZ=0 NormalX=0 NormalY=0 NormalZ=1 AngleXU=0 Radius=1.05
    g6: Circle CenterX=-10.25 CenterY=19.5 CenterZ=0 NormalX=0 NormalY=0 NormalZ=1 AngleXU=0 Radius=1.05
    g7: Circle CenterX=10.25 CenterY=6 CenterZ=0 NormalX=0 NormalY=0 NormalZ=1 AngleXU=0 Radius=1.05
    g8: Circle CenterX=10.25 CenterY=19.5 CenterZ=0 NormalX=0 NormalY=0 NormalZ=1 AngleXU=0 Radius=1.05
    g9: LineSegment StartX=-10 StartY=33.5 StartZ=0 EndX=10 EndY=33.5 EndZ=0
    g10: LineSegment StartX=10 StartY=33.5 StartZ=0 EndX=10 EndY=36.5 EndZ=0
    g11: LineSegment StartX=10 StartY=36.5 StartZ=0 EndX=-10 EndY=36.5 EndZ=0
    g12: LineSegment StartX=-10 StartY=36.5 StartZ=0 EndX=-10 EndY=33.5 EndZ=0
    g13: GeomPoint [constr] X=0 Y=35 Z=0
  constraints (34):
    c: Coincident(g0,g1)
    c: Coincident(g1,g2)
    c: Coincident(g2,g3)
    c: Coincident(g3,g0)
    c: Horizontal(g0)
    c: Horizontal(g2)
    c: Vertical(g1)
    c: Vertical(g3)
    c: Symmetric(g2,g0,g4)
    c: PointOnObject(g4,g-2)
    c: Diameter(g5) = 2.1
    c: Coincident(g6,g2)
    c: Coincident(g7,g0)
    c: Coincident(g8,g1)
    c: Equal(g5,g6)
    c: Equal(g5,g7)
    c: Equal(g6,g8)
    c: DistanceX(g0,g0) = 20.5
    c: DistanceY(g3,g3) = 13.5
    c: Distance(g0,g-3) = 3
    c: Coincident(g5,g0)
    c: Coincident(g9,g10)
    c: Coincident(g10,g11)
    c: Coincident(g11,g12)
    c: Coincident(g12,g9)
    c: Horizontal(g9)
    c: Horizontal(g11)
    c: Vertical(g10)
    c: Vertical(g12)
    c: Symmetric(g11,g9,g13)
    c: PointOnObject(g13,g-2)
    c: DistanceX(g9,g9) = 20
    c: DistanceY(g12,g12) = 3
    c: DistanceY(g2,g9) = 14
FEATURE [PartDesign::Pocket] Pocket
  BaseFeature = -> Chamfer
  Direction = (0,-1,2e-16)
  Length = 0
  Length2 = 5
  Profile = -> Sketch003
  ReferenceAxis = -> Sketch003 [N_Axis]
  Refine = true
  Suppressed = false
  Type = 3
  UpToFace = -> Chamfer [Face6]
FEATURE [Sketcher::SketchObject] Sketch004
  ArcFitTolerance = 1e-06
  AttachmentSupport = -> [Pocket]
  ExternalGeometry = -> [Binder001,Sketch,Sketch001]
  FullyConstrained = true
  MakeInternals = false
  MapMode = 5
  Placement = pos=(0,0,0) rot=(1,0,0;3.14159rad)
  sketch-geometry (8):
    g0: LineSegment StartX=-8 StartY=2.75 StartZ=0 EndX=-11.3 EndY=4 EndZ=0
    g1: LineSegment StartX=-11.3 StartY=4 StartZ=0 EndX=-6 EndY=23.75 EndZ=0
    g2: LineSegment StartX=-6 StartY=23.75 StartZ=0 EndX=6 EndY=23.75 EndZ=0
    g3: LineSegment StartX=6 StartY=23.75 StartZ=0 EndX=11.3 EndY=4 EndZ=0
    g4: LineSegment StartX=11.3 StartY=4 StartZ=0 EndX=8 EndY=2.75 EndZ=0
    g5: LineSegment StartX=-8 StartY=2.75 StartZ=0 EndX=-6 EndY=-4.65 EndZ=0
    g6: LineSegment StartX=-6 StartY=-4.65 StartZ=0 EndX=6 EndY=-4.65 EndZ=0
    g7: LineSegment StartX=6 StartY=-4.65 StartZ=0 EndX=8 EndY=2.75 EndZ=0
  constraints (16):
    c: Coincident(g0,g-7)
    c: Coincident(g1,g0)
    c: Coincident(g1,g-8)
    c: Coincident(g2,g1)
    c: Coincident(g2,g-9)
    c: Coincident(g3,g2)
    c: Coincident(g3,g-9)
    c: Coincident(g4,g3)
    c: Coincident(g4,g-6)
    c: Coincident(g0,g-4)
    c: Coincident(g5,g0)
    c: Coincident(g5,g-11)
    c: Coincident(g6,g5)
    c: Coincident(g6,g-12)
    c: Coincident(g7,g6)
    c: Coincident(g7,g4)
FEATURE [PartDesign::Pocket] Pocket001
  BaseFeature = -> Pocket
  Direction = (0,0,1)
  Length = 1
  Length2 = 5
  Profile = -> Sketch004
  ReferenceAxis = -> Sketch004 [N_Axis]
  Refine = true
  Suppressed = false
  Type = 0
FEATURE [PartDesign::Body] Body  label="FrontCoverBody"
  AllowCompound = false
  Group = -> [Binder,Binder001,Sketch,Pad,Sketch001,Pad001,Sketch002,Pad002,Chamfer,Sketch003,Pocket,Sketch004,Pocket001]
  Origin = -> Origin001
  Tip = -> Pocket001
FEATURE [App::Part] Part  label="FrontCoverPart"
  Group = -> [Body]
  Origin = -> Origin
---- part ../Parts/FrontWheelAxle/FrontWheelAxleLeft.FCStd = doc fcstd_68c86e5070d7 ----
FCSTD DOCUMENT  (FreeCAD 1.0R39285 (Git))
Label: FrontWheelAxleLeft
License: All rights reserved
LicenseURL: https://en.wikipedia.org/wiki/All_rights_reserved
objects: Sketcher::SketchObject×5, PartDesign::Pad×4, PartDesign::Chamfer×3, PartDesign::Pocket×1, PartDesign::Body×1, App::Part×1
note: 35 computed .brp shape members not serialized (recipe doc carries the construction recipe); baked Part::Feature solids carry a one-line shape summary decoded from their .brp

FEATURE [Sketcher::SketchObject] Sketch
  ArcFitTolerance = 1e-06
  AttachmentSupport = -> [YZ_Plane001]
  FullyConstrained = true
  MakeInternals = false
  MapMode = 5
  Placement = pos=(0,0,0) rot=(0.57735,0.57735,0.57735;2.0944rad)
  sketch-geometry (4):
    g0: ArcOfCircle CenterX=0 CenterY=0 CenterZ=0 NormalX=0 NormalY=0 NormalZ=1 AngleXU=0 Radius=4.525 StartAngle=2.80371 EndAngle=3.47948
    g1: ArcOfCircle CenterX=0 CenterY=0 CenterZ=0 NormalX=0 NormalY=0 NormalZ=1 AngleXU=0 Radius=4.525 StartAngle=5.9453 EndAngle=6.62107
    g2: LineSegment StartX=-4.26915 StartY=1.5 StartZ=0 EndX=4.26915 EndY=1.5 EndZ=0
    g3: LineSegment StartX=4.26915 StartY=-1.5 StartZ=0 EndX=-4.26915 EndY=-1.5 EndZ=0
  constraints (12):
    c: Coincident(g0,g-1)
    c: Coincident(g1,g0)
    c: Coincident(g2,g0)
    c: Coincident(g2,g1)
    c: Horizontal(g2)
    c: Coincident(g3,g1)
    c: Coincident(g3,g0)
    c: Horizontal(g3)
    c: Equal(g0,g1)
    c: Equal(g3,g2)
    c: Diameter(g0) = 9.05
    c: Distance(g2,g3) = 3
FEATURE [PartDesign::Pad] Pad
  Direction = (1,0,0)
  Length = 11
  Length2 = 10
  Placement = pos=(0,0,0) rot=(1,1,1;2.0944rad)
  Profile = -> Sketch
  ReferenceAxis = -> Sketch [N_Axis]
  Refine = true
  Reversed = true
  Suppressed = false
  Type = 0
FEATURE [Sketcher::SketchObject] Sketch001
  ArcFitTolerance = 1e-06
  AttachmentSupport = -> [Pad]
  ExternalGeometry = -> [Sketch]
  FullyConstrained = true
  MakeInternals = false
  MapMode = 5
  Placement = pos=(-11,0,0) rot=(0.57735,0.57735,-0.57735;4.18879rad)
  sketch-geometry (1):
    g0: Circle CenterX=0 CenterY=0 CenterZ=0 NormalX=0 NormalY=0 NormalZ=1 AngleXU=0 Radius=4.525
  constraints (2):
    c: Coincident(g0,g-1)
    c: Equal(g0,g-3)
FEATURE [PartDesign::Pad] Pad001
  BaseFeature = -> Pad
  Direction = (-1,0,0)
  Length = 3
  Length2 = 10
  Placement = pos=(0,0,0) rot=(1,1,1;2.0944rad)
  Profile = -> Sketch001
  ReferenceAxis = -> Sketch001 [N_Axis]
  Refine = true
  Suppressed = false
  Type = 0
FEATURE [Sketcher::SketchObject] Sketch002
  ArcFitTolerance = 1e-06
  AttachmentSupport = -> [Pad001]
  FullyConstrained = true
  MakeInternals = false
  MapMode = 5
  Placement = pos=(-14,0,0) rot=(0.57735,0.57735,-0.57735;4.18879rad)
  sketch-geometry (1):
    g0: Circle CenterX=0 CenterY=0 CenterZ=0 NormalX=0 NormalY=0 NormalZ=1 AngleXU=0 Radius=6.5
  constraints (2):
    c: Coincident(g0,g-1)
    c: Diameter(g0) = 13
FEATURE [PartDesign::Pad] Pad002
  BaseFeature = -> Pad001
  Direction = (-1,0,0)
  Length = 2
  Length2 = 10
  Placement = pos=(0,0,0) rot=(1,1,1;2.0944rad)
  Profile = -> Sketch002
  ReferenceAxis = -> Sketch002 [N_Axis]
  Refine = true
  Suppressed = false
  Type = 0
FEATURE [Sketcher::SketchObject] Sketch003
  ArcFitTolerance = 1e-06
  AttachmentSupport = -> [Pad002]
  ExternalGeometry = -> [Sketch]
  FullyConstrained = true
  MakeInternals = false
  MapMode = 5
  Placement = pos=(-16,0,0) rot=(0.57735,0.57735,-0.57735;4.18879rad)
  sketch-geometry (1):
    g0: Circle CenterX=0 CenterY=0 CenterZ=0 NormalX=0 NormalY=0 NormalZ=1 AngleXU=0 Radius=4.525
  constraints (2):
    c: Coincident(g0,g-1)
    c: Equal(g0,g-3)
FEATURE [PartDesign::Pad] Pad003
  BaseFeature = -> Pad002
  Direction = (-1,0,0)
  Length = 10
  Length2 = 10
  Placement = pos=(0,0,0) rot=(1,1,1;2.0944rad)
  Profile = -> Sketch003
  ReferenceAxis = -> Sketch003 [N_Axis]
  Refine = true
  Suppressed = false
  Type = 0
FEATURE [Sketcher::SketchObject] Sketch004
  ArcFitTolerance = 1e-06
  AttachmentSupport = -> [Pad003]
  FullyConstrained = true
  MakeInternals = false
  MapMode = 5
  Placement = pos=(0,3e-16,1.5) rot=(0,0,-1;1.5708rad)
  sketch-geometry (2):
    g0: Circle CenterX=0 CenterY=-3 CenterZ=0 NormalX=0 NormalY=0 NormalZ=1 AngleXU=0 Radius=1.62
    g1: Circle CenterX=0 CenterY=-8 CenterZ=0 NormalX=0 NormalY=0 NormalZ=1 AngleXU=0 Radius=1.68
  constraints (6):
    c: Diameter(g0) = 3.24
    c: PointOnObject(g0,g-2)
    c: DistanceY(g0,g-1) = 3
    c: Diameter(g1) = 3.36
    c: PointOnObject(g1,g-2)
    c: DistanceY(g1,g0) = 5
FEATURE [PartDesign::Pocket] Pocket
  BaseFeature = -> Pad003
  Direction = (0,0,-1)
  Length = 0
  Length2 = 5
  Placement = pos=(0,0,0) rot=(1,1,1;2.0944rad)
  Profile = -> Sketch004
  ReferenceAxis = -> Sketch004 [N_Axis]
  Refine = true
  Suppressed = false
  Type = 3
  UpToFace = -> Pad003 [Face5]
FEATURE [PartDesign::Chamfer] Chamfer
  Angle = 45
  Base = -> Pocket [Edge27]
  BaseFeature = -> Pocket
  ChamferType = 1
  FlipDirection = false
  Placement = pos=(0,0,0) rot=(1,1,1;2.0944rad)
  Refine = true
  Size = 2
  Size2 = 1
  SupportTransform = false
  Suppressed = false
  UseAllEdges = false
FEATURE [PartDesign::Chamfer] Chamfer001
  Angle = 45
  Base = -> Chamfer [Edge10]
  BaseFeature = -> Chamfer
  ChamferType = 1
  FlipDirection = false
  Placement = pos=(0,0,0) rot=(1,1,1;2.0944rad)
  Refine = true
  Size = 9
  Size2 = 2.2
  SupportTransform = false
  Suppressed = false
  UseAllEdges = false
FEATURE [PartDesign::Chamfer] Chamfer002
  Angle = 45
  Base = -> Chamfer001 [Edge10,Edge7]
  BaseFeature = -> Chamfer001
  ChamferType = 1
  FlipDirection = false
  Placement = pos=(0,0,0) rot=(1,1,1;2.0944rad)
  Refine = true
  Size = 3
  Size2 = 2
  SupportTransform = false
  Suppressed = false
  UseAllEdges = false
FEATURE [PartDesign::Body] Body  label="FrontWheelAxleLeftBody"
  AllowCompound = false
  Group = -> [Sketch,Pad,Sketch001,Pad001,Sketch002,Pad002,Sketch003,Pad003,Sketch004,Pocket,Chamfer,Chamfer001,Chamfer002]
  Origin = -> Origin001
  Tip = -> Chamfer002
FEATURE [App::Part] Part  label="FrontWheelAxleLeftPart"
  Group = -> [Body]
  Origin = -> Origin
---- part ../Parts/FrontWheelAxle/FrontWheelAxleRight.FCStd = doc fcstd_31e5d270f517 ----
FCSTD DOCUMENT  (FreeCAD 1.0R39285 (Git))
Label: FrontWheelAxleRight
License: All rights reserved
LicenseURL: https://en.wikipedia.org/wiki/All_rights_reserved
objects: PartDesign::SubShapeBinder×1, Part::Mirroring×1, App::Part×1
note: 2 computed .brp shape members not serialized (recipe doc carries the construction recipe); baked Part::Feature solids carry a one-line shape summary decoded from their .brp
EXTERNAL_REF file=FrontWheelAxleLeft.FCStd obj=Part

FEATURE [PartDesign::SubShapeBinder] Binder  label="FrontWheelAxleLeftBody"
  BindCopyOnChange = 0
  BindMode = 0
  ClaimChildren = false
  Context = -> Part [Binder.]
  Fuse = false
  MakeFace = true
  OffsetFill = false
  OffsetIntersection = false
  OffsetJoinType = 0
  OffsetOpenResult = false
  PartialLoad = false
  Refine = true
  Relative = true
  Support = -> [<external FrontWheelAxleLeft.FCStd>#Part[Body.]]
  _Version = 2
FEATURE [Part::Mirroring] Part__Mirroring  label="FrontWheelAxleRightBody"
  Base = (0,0,0)
  Normal = (1,0,0)
  Source = -> Binder
FEATURE [App::Part] Part  label="FrontWheelAxleRightPart"
  Group = -> [Binder,Part__Mirroring]
  Origin = -> Origin
---- part ../Parts/FrontWheelStopper.FCStd = doc fcstd_769df6a6616b ----
FCSTD DOCUMENT  (FreeCAD 1.0R39109 (Git))
Label: FrontWheelStopper
License: All rights reserved
LicenseURL: https://en.wikipedia.org/wiki/All_rights_reserved
objects: Sketcher::SketchObject×2, PartDesign::Pad×2, PartDesign::Fillet×1, PartDesign::Body×1, App::Part×1
note: 14 computed .brp shape members not serialized (recipe doc carries the construction recipe); baked Part::Feature solids carry a one-line shape summary decoded from their .brp

FEATURE [Sketcher::SketchObject] Sketch
  ArcFitTolerance = 1e-06
  AttachmentSupport = -> [YZ_Plane001]
  FullyConstrained = true
  MakeInternals = false
  MapMode = 5
  Placement = pos=(0,0,0) rot=(0.57735,0.57735,0.57735;2.0944rad)
  sketch-geometry (12):
    g0: LineSegment [constr] StartX=0 StartY=10 StartZ=0 EndX=-8.66025 EndY=-5 EndZ=0
    g1: LineSegment [constr] StartX=-8.66025 StartY=-5 StartZ=0 EndX=8.66025 EndY=-5 EndZ=0
    g2: LineSegment [constr] StartX=8.66025 StartY=-5 StartZ=0 EndX=0 EndY=10 EndZ=0
    g3: Circle [constr] CenterX=0 CenterY=0 CenterZ=0 NormalX=0 NormalY=0 NormalZ=1 AngleXU=0 Radius=10
    g4: LineSegment StartX=0 StartY=20.2073 StartZ=0 EndX=-17.5 EndY=-10.1036 EndZ=0
    g5: LineSegment StartX=-17.5 StartY=-10.1036 StartZ=0 EndX=17.5 EndY=-10.1036 EndZ=0
    g6: LineSegment StartX=17.5 StartY=-10.1036 StartZ=0 EndX=0 EndY=20.2073 EndZ=0
    g7: Circle [constr] CenterX=0 CenterY=0 CenterZ=0 NormalX=0 NormalY=0 NormalZ=1 AngleXU=0 Radius=20.2073
    g8: Circle CenterX=0 CenterY=0 CenterZ=0 NormalX=0 NormalY=0 NormalZ=1 AngleXU=0 Radius=4.725
    g9: Circle CenterX=0 CenterY=10 CenterZ=0 NormalX=0 NormalY=0 NormalZ=1 AngleXU=0 Radius=1.5
    g10: Circle CenterX=-8.66025 CenterY=-5 CenterZ=0 NormalX=0 NormalY=0 NormalZ=1 AngleXU=0 Radius=1.5
    g11: Circle CenterX=8.66025 CenterY=-5 CenterZ=0 NormalX=0 NormalY=0 NormalZ=1 AngleXU=0 Radius=1.5
  constraints (30):
    c: Coincident(g0,g1)
    c: Coincident(g1,g2)
    c: Coincident(g2,g0)
    c: Equal(g0,g1)
    c: Equal(g0,g2)
    c: PointOnObject(g0,g3)
    c: PointOnObject(g1,g3)
    c: PointOnObject(g2,g3)
    c: Coincident(g3,g-1)
    c: PointOnObject(g2,g-2)
    c: DistanceY(g3,g0) = 10
    c: Coincident(g4,g5)
    c: Coincident(g5,g6)
    c: Coincident(g6,g4)
    c: Equal(g4,g5)
    c: Equal(g4,g6)
    c: PointOnObject(g4,g7)
    c: PointOnObject(g5,g7)
    c: PointOnObject(g6,g7)
    c: Coincident(g7,g3)
    c: PointOnObject(g6,g-2)
    c: DistanceX(g5,g5) = 35
    c: Diameter(g8) = 9.45
    c: Coincident(g8,g3)
    c: Diameter(g9) = 3
    c: Coincident(g9,g0)
    c: Coincident(g10,g0)
    c: Coincident(g11,g1)
    c: Diameter(g10) = 3
    c: Diameter(g11) = 3
FEATURE [PartDesign::Pad] Pad
  Direction = (1,0,0)
  Length = 2
  Length2 = 10
  Placement = pos=(0,0,0) rot=(1,1,1;2.0944rad)
  Profile = -> Sketch
  ReferenceAxis = -> Sketch [N_Axis]
  Refine = true
  Reversed = true
  Suppressed = false
  Type = 0
FEATURE [Sketcher::SketchObject] Sketch001
  ArcFitTolerance = 1e-06
  AttachmentSupport = -> [Pad]
  ExternalGeometry = -> [Sketch]
  FullyConstrained = true
  MakeInternals = false
  MapMode = 5
  Placement = pos=(-2,4e-16,-2e-16) rot=(0.57735,0.57735,-0.57735;4.18879rad)
  sketch-geometry (6):
    g0: Circle CenterX=-8.66025 CenterY=5 CenterZ=0 NormalX=0 NormalY=0 NormalZ=1 AngleXU=0 Radius=1.5
    g1: Circle CenterX=8.66025 CenterY=5 CenterZ=0 NormalX=0 NormalY=0 NormalZ=1 AngleXU=0 Radius=1.5
    g2: Circle CenterX=0 CenterY=-10 CenterZ=0 NormalX=0 NormalY=0 NormalZ=1 AngleXU=0 Radius=1.5
    g3: Circle CenterX=8.66025 CenterY=5 CenterZ=0 NormalX=0 NormalY=0 NormalZ=1 AngleXU=0 Radius=3
    g4: Circle CenterX=-8.66025 CenterY=5 CenterZ=0 NormalX=0 NormalY=0 NormalZ=1 AngleXU=0 Radius=3
    g5: Circle CenterX=0 CenterY=-10 CenterZ=0 NormalX=0 NormalY=0 NormalZ=1 AngleXU=0 Radius=3
  constraints (12):
    c: Coincident(g0,g-5)
    c: Coincident(g1,g-4)
    c: Coincident(g2,g-3)
    c: Equal(g1,g-4)
    c: Equal(g0,g-5)
    c: Equal(g2,g-3)
    c: Coincident(g3,g1)
    c: Coincident(g4,g0)
    c: Coincident(g5,g2)
    c: Diameter(g3) = 6
    c: Diameter(g4) = 6
    c: Diameter(g5) = 6
FEATURE [PartDesign::Pad] Pad001
  BaseFeature = -> Pad
  Direction = (-1,0,0)
  Length = 4
  Length2 = 10
  Placement = pos=(0,0,0) rot=(1,1,1;2.0944rad)
  Profile = -> Sketch001
  ReferenceAxis = -> Sketch001 [N_Axis]
  Refine = true
  Suppressed = false
  Type = 0
FEATURE [PartDesign::Fillet] Fillet
  Base = -> Pad001 [Edge1,Edge2,Edge5]
  BaseFeature = -> Pad001
  Placement = pos=(0,0,0) rot=(1,1,1;2.0944rad)
  Radius = 6
  Refine = true
  SupportTransform = false
  Suppressed = false
  UseAllEdges = false
FEATURE [PartDesign::Body] Body  label="FrontWheelStopperBody"
  AllowCompound = false
  Group = -> [Sketch,Pad,Sketch001,Pad001,Fillet]
  Origin = -> Origin001
  Tip = -> Fillet
FEATURE [App::Part] Part  label="FrontWheelStopperPart"
  Group = -> [Body]
  Origin = -> Origin
---- part ../Parts/S0004m.FCStd = doc fcstd_35093f32faee ----
FCSTD DOCUMENT  (FreeCAD 1.0R39109 (Git))
Label: S0004m
License: All rights reserved
LicenseURL: https://en.wikipedia.org/wiki/All_rights_reserved
objects: Sketcher::SketchObject×5, PartDesign::Pad×5, PartDesign::Body×1, App::Part×1
note: 26 computed .brp shape members not serialized (recipe doc carries the construction recipe); baked Part::Feature solids carry a one-line shape summary decoded from their .brp

FEATURE [Sketcher::SketchObject] Sketch
  ArcFitTolerance = 1e-06
  AttachmentSupport = -> [XY_Plane001]
  FullyConstrained = true
  MakeInternals = false
  MapMode = 5
  sketch-geometry (5):
    g0: LineSegment StartX=-4.25 StartY=-10.1 StartZ=0 EndX=4.25 EndY=-10.1 EndZ=0
    g1: LineSegment StartX=4.25 StartY=-10.1 StartZ=0 EndX=4.25 EndY=10.1 EndZ=0
    g2: LineSegment StartX=4.25 StartY=10.1 StartZ=0 EndX=-4.25 EndY=10.1 EndZ=0
    g3: LineSegment StartX=-4.25 StartY=10.1 StartZ=0 EndX=-4.25 EndY=-10.1 EndZ=0
    g4: GeomPoint [constr] X=0 Y=0 Z=0
  constraints (12):
    c: Coincident(g0,g1)
    c: Coincident(g1,g2)
    c: Coincident(g2,g3)
    c: Coincident(g3,g0)
    c: Horizontal(g0)
    c: Horizontal(g2)
    c: Vertical(g1)
    c: Vertical(g3)
    c: Symmetric(g2,g0,g4)
    c: Distance(g1,g3) = 8.5
    c: Distance(g0,g2) = 20.2
    c: Coincident(g4,g-1)
FEATURE [PartDesign::Pad] Pad
  Direction = (0,0,1)
  Length = 15.2
  Length2 = 10
  Profile = -> Sketch
  ReferenceAxis = -> Sketch [N_Axis]
  Refine = true
  Suppressed = false
  Type = 0
FEATURE [Sketcher::SketchObject] Sketch001
  ArcFitTolerance = 1e-06
  AttachmentSupport = -> [Pad]
  ExternalGeometry = -> [Pad]
  FullyConstrained = true
  MakeInternals = false
  MapMode = 5
  Placement = pos=(0,0,15.2) rot=(0,0,1;0rad)
  sketch-geometry (10):
    g0: LineSegment StartX=4.25 StartY=10.1 StartZ=0 EndX=4.25 EndY=13.6 EndZ=0
    g1: LineSegment StartX=4.25 StartY=13.6 StartZ=0 EndX=-4.25 EndY=13.6 EndZ=0
    g2: LineSegment StartX=-4.25 StartY=13.6 StartZ=0 EndX=-4.25 EndY=10.1 EndZ=0
    g3: LineSegment StartX=-4.25 StartY=-10.1 StartZ=0 EndX=-4.25 EndY=-13.6 EndZ=0
    g4: LineSegment StartX=-4.25 StartY=-13.6 StartZ=0 EndX=4.25 EndY=-13.6 EndZ=0
    g5: LineSegment StartX=4.25 StartY=-13.6 StartZ=0 EndX=4.25 EndY=-10.1 EndZ=0
    g6: Circle CenterX=0 CenterY=11.8 CenterZ=0 NormalX=0 NormalY=0 NormalZ=1 AngleXU=0 Radius=1
    g7: Circle CenterX=0 CenterY=-11.8 CenterZ=0 NormalX=0 NormalY=0 NormalZ=1 AngleXU=0 Radius=1
    g8: LineSegment StartX=-4.25 StartY=10.1 StartZ=0 EndX=-4.25 EndY=-10.1 EndZ=0
    g9: LineSegment StartX=4.25 StartY=-10.1 StartZ=0 EndX=4.25 EndY=10.1 EndZ=0
  constraints (25):
    c: Coincident(g0,g1)
    c: Coincident(g1,g2)
    c: Horizontal(g1)
    c: Vertical(g0)
    c: Vertical(g2)
    c: Coincident(g2,g-3)
    c: Coincident(g0,g-4)
    c: Coincident(g3,g4)
    c: Coincident(g4,g5)
    c: Vertical(g3)
    c: Vertical(g5)
    c: Horizontal(g4)
    c: Coincident(g-3,g3)
    c: Coincident(g-4,g5)
    c: Equal(g2,g3)
    c: DistanceY(g2,g2) = 3.5
    c: PointOnObject(g6,g-2)
    c: Diameter(g6) = 2
    c: Equal(g6,g7)
    c: Symmetric(g6,g7,g-1)
    c: DistanceY(g2,g6) = 1.7
    c: Coincident(g8,g2)
    c: Coincident(g8,g3)
    c: Coincident(g9,g5)
    c: Coincident(g9,g0)
FEATURE [PartDesign::Pad] Pad001
  BaseFeature = -> Pad
  Direction = (0,0,1)
  Length = 0.8
  Length2 = 10
  Profile = -> Sketch001
  ReferenceAxis = -> Sketch001 [N_Axis]
  Refine = true
  Suppressed = false
  Type = 0
FEATURE [Sketcher::SketchObject] Sketch002
  ArcFitTolerance = 1e-06
  AttachmentSupport = -> [Pad001]
  ExternalGeometry = -> [Pad001]
  FullyConstrained = true
  MakeInternals = false
  MapMode = 5
  Placement = pos=(0,0,16) rot=(0,0,1;0rad)
  sketch-geometry (4):
    g0: LineSegment StartX=-4.25 StartY=10.1 StartZ=0 EndX=-4.25 EndY=-10.1 EndZ=0
    g1: LineSegment StartX=-4.25 StartY=-10.1 StartZ=0 EndX=4.25 EndY=-10.1 EndZ=0
    g2: LineSegment StartX=4.25 StartY=-10.1 StartZ=0 EndX=4.25 EndY=10.1 EndZ=0
    g3: LineSegment StartX=4.25 StartY=10.1 StartZ=0 EndX=-4.25 EndY=10.1 EndZ=0
  constraints (10):
    c: Coincident(g0,g1)
    c: Coincident(g1,g2)
    c: Coincident(g2,g3)
    c: Coincident(g3,g0)
    c: Vertical(g0)
    c: Vertical(g2)
    c: Horizontal(g1)
    c: Horizontal(g3)
    c: Coincident(g0,g-6)
    c: Coincident(g1,g-5)
FEATURE [PartDesign::Pad] Pad002
  BaseFeature = -> Pad001
  Direction = (0,0,1)
  Length = 3.5
  Length2 = 10
  Profile = -> Sketch002
  ReferenceAxis = -> Sketch002 [N_Axis]
  Refine = true
  Suppressed = false
  Type = 0
FEATURE [Sketcher::SketchObject] Sketch003
  ArcFitTolerance = 1e-06
  AttachmentSupport = -> [Pad002]
  ExternalGeometry = -> [Pad002]
  FullyConstrained = true
  MakeInternals = false
  MapMode = 5
  Placement = pos=(0,0,19.5) rot=(0,0,1;0rad)
  sketch-geometry (1):
    g0: Circle CenterX=0 CenterY=-5.55 CenterZ=0 NormalX=0 NormalY=0 NormalZ=1 AngleXU=0 Radius=4.25
  constraints (3):
    c: Diameter(g0) = 8.5
    c: PointOnObject(g0,g-2)
    c: Distance(g0,g-3) = 4.55
FEATURE [PartDesign::Pad] Pad003
  BaseFeature = -> Pad002
  Direction = (0,0,1)
  Length = 4.5
  Length2 = 10
  Profile = -> Sketch003
  ReferenceAxis = -> Sketch003 [N_Axis]
  Refine = true
  Suppressed = false
  Type = 0
FEATURE [Sketcher::SketchObject] Sketch004
  ArcFitTolerance = 1e-06
  AttachmentSupport = -> [Pad003]
  ExternalGeometry = -> [Pad003]
  FullyConstrained = true
  MakeInternals = false
  MapMode = 5
  Placement = pos=(0,0,24) rot=(0,0,1;0rad)
  sketch-geometry (1):
    g0: Circle CenterX=0 CenterY=-5.55 CenterZ=0 NormalX=0 NormalY=0 NormalZ=1 AngleXU=0 Radius=1.85
  constraints (2):
    c: Diameter(g0) = 3.7
    c: Coincident(g0,g-3)
FEATURE [PartDesign::Pad] Pad004
  BaseFeature = -> Pad003
  Direction = (0,0,1)
  Length = 2.5
  Length2 = 10
  Profile = -> Sketch004
  ReferenceAxis = -> Sketch004 [N_Axis]
  Refine = true
  Suppressed = false
  Type = 0
FEATURE [PartDesign::Body] Body  label="S0004mBody"
  AllowCompound = false
  Group = -> [Sketch,Pad,Sketch001,Pad001,Sketch002,Pad002,Sketch003,Pad003,Sketch004,Pad004]
  Origin = -> Origin001
  Tip = -> Pad004
FEATURE [App::Part] Part  label="S0004mPart"
  Group = -> [Body]
  Origin = -> Origin
---- part ../Parts/TBoneLinkage/TBoneLinkageBottom.FCStd = doc fcstd_ef4fcdcf9c16 ----
FCSTD DOCUMENT  (FreeCAD 1.0R39285 (Git))
Label: TBoneLinkageBottom
License: All rights reserved
LicenseURL: https://en.wikipedia.org/wiki/All_rights_reserved
objects: Sketcher::SketchObject×5, PartDesign::Pad×4, App::Link×1, PartDesign::Pocket×1, PartDesign::Body×1, App::Part×1
note: 26 computed .brp shape members not serialized (recipe doc carries the construction recipe); baked Part::Feature solids carry a one-line shape summary decoded from their .brp
EXTERNAL_REF file=../../Models/SteeringAckermannModel.FCStd obj=Spreadsheet

FEATURE [App::Link] Link  label="SteeringAckermannSpreadsheet"
  LinkedObject = -> <external ../../Models/SteeringAckermannModel.FCStd>#Spreadsheet
FEATURE [Sketcher::SketchObject] Sketch
  ArcFitTolerance = 1e-06
  AttachmentSupport = -> [XY_Plane001]
  FullyConstrained = true
  MakeInternals = false
  MapMode = 5
  expr: Constraints[4] = <<SteeringAckermannSpreadsheet>>.servolinkagelength
  expr: Constraints[5] = <<SteeringAckermannSpreadsheet>>.servolinkagesep
  sketch-geometry (8):
    g0: LineSegment [constr] StartX=0 StartY=0 StartZ=0 EndX=0 EndY=-12 EndZ=0
    g1: LineSegment [constr] StartX=-5 StartY=-12 StartZ=0 EndX=5 EndY=-12 EndZ=0
    g2: ArcOfCircle CenterX=0 CenterY=0 CenterZ=0 NormalX=0 NormalY=0 NormalZ=1 AngleXU=0 Radius=4.1 StartAngle=0.394791 EndAngle=2.7468
    g3: ArcOfCircle CenterX=-5 CenterY=-12 CenterZ=0 NormalX=0 NormalY=0 NormalZ=1 AngleXU=0 Radius=4.1 StartAngle=2.7468 EndAngle=4.71239
    g4: ArcOfCircle CenterX=5 CenterY=-12 CenterZ=0 NormalX=0 NormalY=0 NormalZ=1 AngleXU=0 Radius=4.1 StartAngle=4.71239 EndAngle=6.67798
    g5: LineSegment StartX=-8.78462 StartY=-10.4231 StartZ=0 EndX=-3.78462 EndY=1.57692 EndZ=0
    g6: LineSegment StartX=3.78462 StartY=1.57692 StartZ=0 EndX=8.78462 EndY=-10.4231 EndZ=0
    g7: LineSegment StartX=5 StartY=-16.1 StartZ=0 EndX=-5 EndY=-16.1 EndZ=0
  constraints (18):
    c: Coincident(g0,g-1)
    c: Vertical(g0)
    c: Symmetric(g1,g1,g0)
    c: Horizontal(g1)
    c: DistanceY(g0,g0) = 12
    c: DistanceX(g1,g1) = 10
    c: Coincident(g2,g0)
    c: Coincident(g3,g1)
    c: Coincident(g4,g1)
    c: Horizontal(g7)
    c: Tangent(g5,g2) = 1.5708
    c: Tangent(g5,g3) = 1.5708
    c: Tangent(g7,g3) = 1.5708
    c: Tangent(g7,g4) = 1.5708
    c: Tangent(g6,g4) = 1.5708
    c: Tangent(g6,g2) = 1.5708
    c: Radius(g2) = 4.1
    c: Radius(g3) = 4.1
FEATURE [PartDesign::Pad] Pad
  Direction = (0,0,1)
  Length = 2
  Length2 = 10
  Profile = -> Sketch
  ReferenceAxis = -> Sketch [N_Axis]
  Refine = true
  Suppressed = false
  Type = 0
FEATURE [Sketcher::SketchObject] Sketch001
  ArcFitTolerance = 1e-06
  AttachmentSupport = -> [Pad]
  ExternalGeometry = -> [Sketch]
  FullyConstrained = true
  MakeInternals = false
  MapMode = 5
  Placement = pos=(0,0,2) rot=(0,0,1;0rad)
  sketch-geometry (2):
    g0: Circle CenterX=-5 CenterY=-12 CenterZ=0 NormalX=0 NormalY=0 NormalZ=1 AngleXU=0 Radius=2.5
    g1: Circle CenterX=5 CenterY=-12 CenterZ=0 NormalX=0 NormalY=0 NormalZ=1 AngleXU=0 Radius=2.5
  constraints (4):
    c: Coincident(g0,g-3)
    c: Coincident(g1,g-4)
    c: Diameter(g0) = 5
    c: Equal(g0,g1)
FEATURE [PartDesign::Pad] Pad001
  BaseFeature = -> Pad
  Direction = (0,0,1)
  Length = 0.5
  Length2 = 10
  Profile = -> Sketch001
  ReferenceAxis = -> Sketch001 [N_Axis]
  Refine = true
  Suppressed = false
  Type = 0
FEATURE [Sketcher::SketchObject] Sketch002
  ArcFitTolerance = 1e-06
  AttachmentSupport = -> [Pad001]
  ExternalGeometry = -> [Sketch]
  FullyConstrained = true
  MakeInternals = false
  MapMode = 5
  Placement = pos=(0,0,2.5) rot=(0,0,1;0rad)
  sketch-geometry (2):
    g0: Circle CenterX=-5 CenterY=-12 CenterZ=0 NormalX=0 NormalY=0 NormalZ=1 AngleXU=0 Radius=1.5
    g1: Circle CenterX=5 CenterY=-12 CenterZ=0 NormalX=0 NormalY=0 NormalZ=1 AngleXU=0 Radius=1.5
  constraints (4):
    c: Diameter(g0) = 3
    c: Coincident(g0,g-3)
    c: Coincident(g1,g-4)
    c: Equal(g0,g1)
FEATURE [PartDesign::Pad] Pad002
  BaseFeature = -> Pad001
  Direction = (0,0,1)
  Length = 4.5
  Length2 = 10
  Profile = -> Sketch002
  ReferenceAxis = -> Sketch002 [N_Axis]
  Refine = true
  Suppressed = false
  Type = 0
FEATURE [Sketcher::SketchObject] Sketch003
  ArcFitTolerance = 1e-06
  AttachmentSupport = -> [Pad002]
  ExternalGeometry = -> [Sketch]
  FullyConstrained = true
  MakeInternals = false
  MapMode = 5
  Placement = pos=(0,0,2) rot=(0,0,1;0rad)
  sketch-geometry (6):
    g0: ArcOfCircle CenterX=0 CenterY=0 CenterZ=0 NormalX=0 NormalY=0 NormalZ=1 AngleXU=0 Radius=4.1 StartAngle=0.394791 EndAngle=2.7468
    g1: LineSegment StartX=-3.78462 StartY=1.57692 StartZ=0 EndX=-6.47692 EndY=-4.88462 EndZ=0
    g2: LineSegment StartX=3.78462 StartY=1.57692 StartZ=0 EndX=6.47692 EndY=-4.88462 EndZ=0
    g3: LineSegment StartX=-6.47692 StartY=-4.88462 StartZ=0 EndX=-9e-16 EndY=-7.58333 EndZ=0
    g4: LineSegment StartX=-9e-16 StartY=-7.58333 StartZ=0 EndX=6.47692 EndY=-4.88462 EndZ=0
    g5: Circle CenterX=0 CenterY=0 CenterZ=0 NormalX=0 NormalY=0 NormalZ=1 AngleXU=0 Radius=1
  constraints (14):
    c: Coincident(g0,g-1)
    c: Coincident(g3,g1)
    c: Coincident(g4,g2)
    c: Tangent(g1,g0) = -1.5708
    c: Tangent(g2,g0) = 1.5708
    c: Coincident(g0,g-6)
    c: PointOnObject(g2,g-7)
    c: Equal(g1,g2)
    c: Distance(g1,g1) = 7
    c: Perpendicular(g3,g1)
    c: Coincident(g3,g4)
    c: Equal(g3,g4)
    c: Diameter(g5) = 2
    c: Coincident(g5,g0)
FEATURE [PartDesign::Pad] Pad003
  BaseFeature = -> Pad002
  Direction = (0,0,1)
  Length = 3
  Length2 = 10
  Profile = -> Sketch003
  ReferenceAxis = -> Sketch003 [N_Axis]
  Refine = true
  Suppressed = false
  Type = 0
FEATURE [Sketcher::SketchObject] Sketch004
  ArcFitTolerance = 1e-06
  AttachmentSupport = -> [Pad003]
  ExternalGeometry = -> [Sketch]
  FullyConstrained = true
  MakeInternals = false
  MapMode = 5
  Placement = pos=(0,0,0) rot=(1,0,0;3.14159rad)
  sketch-geometry (1):
    g0: Circle CenterX=0 CenterY=0 CenterZ=0 NormalX=0 NormalY=0 NormalZ=1 AngleXU=0 Radius=2.5
  constraints (2):
    c: Diameter(g0) = 5
    c: Coincident(g0,g-1)
FEATURE [PartDesign::Pocket] Pocket
  BaseFeature = -> Pad003
  Direction = (0,0,1)
  Length = 4
  Length2 = 5
  Profile = -> Sketch004
  ReferenceAxis = -> Sketch004 [N_Axis]
  Refine = true
  Suppressed = false
  Type = 0
FEATURE [PartDesign::Body] Body  label="TBoneLinkageBottomBody"
  AllowCompound = false
  Group = -> [Sketch,Pad,Sketch001,Pad001,Sketch002,Pad002,Sketch003,Pad003,Sketch004,Pocket]
  Origin = -> Origin001
  Tip = -> Pocket
FEATURE [App::Part] Part  label="TBoneLinkageBottomPart"
  Group = -> [Body]
  Origin = -> Origin
---- part ../Parts/TBoneLinkage/TBoneLinkageTop.FCStd = doc fcstd_5407f23f83f5 ----
FCSTD DOCUMENT  (FreeCAD 1.0R39285 (Git))
Label: TBoneLinkageTop
License: All rights reserved
LicenseURL: https://en.wikipedia.org/wiki/All_rights_reserved
objects: Sketcher::SketchObject×2, PartDesign::Pad×2, PartDesign::SubShapeBinder×1, PartDesign::Body×1, App::Part×1
note: 12 computed .brp shape members not serialized (recipe doc carries the construction recipe); baked Part::Feature solids carry a one-line shape summary decoded from their .brp
EXTERNAL_REF file=TBoneLinkageBottom.FCStd obj=Part

FEATURE [PartDesign::SubShapeBinder] Binder  label="TBoneLinkageBottomSketch"
  BindCopyOnChange = 0
  BindMode = 0
  ClaimChildren = false
  Context = -> Part [Body.Binder.]
  Fuse = false
  MakeFace = true
  OffsetFill = false
  OffsetIntersection = false
  OffsetJoinType = 0
  OffsetOpenResult = false
  PartialLoad = false
  Refine = true
  Relative = true
  Support = -> [<external TBoneLinkageBottom.FCStd>#Part[Body.Sketch.]]
  _Version = 2
FEATURE [Sketcher::SketchObject] Sketch
  ArcFitTolerance = 1e-06
  AttachmentSupport = -> [XY_Plane001]
  ExternalGeometry = -> [Binder]
  FullyConstrained = true
  MakeInternals = false
  MapMode = 5
  sketch-geometry (9):
    g0: ArcOfCircle CenterX=0 CenterY=0 CenterZ=0 NormalX=0 NormalY=0 NormalZ=1 AngleXU=0 Radius=4.1 StartAngle=0.394791 EndAngle=2.7468
    g1: ArcOfCircle CenterX=-5 CenterY=-12 CenterZ=0 NormalX=0 NormalY=0 NormalZ=1 AngleXU=0 Radius=4.1 StartAngle=2.7468 EndAngle=4.71239
    g2: ArcOfCircle CenterX=5 CenterY=-12 CenterZ=0 NormalX=0 NormalY=0 NormalZ=1 AngleXU=0 Radius=4.1 StartAngle=4.71239 EndAngle=6.67798
    g3: LineSegment StartX=-3.78462 StartY=1.57692 StartZ=0 EndX=-8.78462 EndY=-10.4231 EndZ=0
    g4: LineSegment StartX=-5.00001 StartY=-16.1 StartZ=0 EndX=5 EndY=-16.1 EndZ=0
    g5: LineSegment StartX=8.78462 StartY=-10.4231 StartZ=0 EndX=3.78462 EndY=1.57692 EndZ=0
    g6: Circle CenterX=-5 CenterY=-12 CenterZ=0 NormalX=0 NormalY=0 NormalZ=1 AngleXU=0 Radius=1.64
    g7: Circle CenterX=5 CenterY=-12 CenterZ=0 NormalX=0 NormalY=0 NormalZ=1 AngleXU=0 Radius=1.64
    g8: Circle CenterX=0 CenterY=0 CenterZ=0 NormalX=0 NormalY=0 NormalZ=1 AngleXU=0 Radius=1.9
  constraints (17):
    c: Coincident(g0,g-1)
    c: Coincident(g1,g-6)
    c: Coincident(g2,g-7)
    c: Coincident(g4,g1)
    c: Tangent(g3,g0) = -1.5708
    c: Tangent(g3,g1) = -1.5708
    c: Tangent(g4,g2) = -1.5708
    c: Tangent(g5,g2) = -1.5708
    c: Tangent(g5,g0) = -1.5708
    c: Coincident(g0,g-5)
    c: Coincident(g2,g-8)
    c: Diameter(g6) = 3.28
    c: Coincident(g6,g1)
    c: Coincident(g7,g2)
    c: Equal(g6,g7)
    c: Diameter(g8) = 3.8
    c: Coincident(g8,g0)
FEATURE [PartDesign::Pad] Pad
  Direction = (0,0,1)
  Length = 2
  Length2 = 10
  Profile = -> Sketch
  ReferenceAxis = -> Sketch [N_Axis]
  Refine = true
  Reversed = true
  Suppressed = false
  Type = 0
FEATURE [Sketcher::SketchObject] Sketch001
  ArcFitTolerance = 1e-06
  AttachmentSupport = -> [Pad]
  ExternalGeometry = -> [Sketch]
  FullyConstrained = true
  MakeInternals = false
  MapMode = 5
  Placement = pos=(0,0,-2) rot=(1,0,0;3.14159rad)
  sketch-geometry (4):
    g0: Circle CenterX=-5 CenterY=12 CenterZ=0 NormalX=0 NormalY=0 NormalZ=1 AngleXU=0 Radius=1.64
    g1: Circle CenterX=5 CenterY=12 CenterZ=0 NormalX=0 NormalY=0 NormalZ=1 AngleXU=0 Radius=1.64
    g2: Circle CenterX=-5 CenterY=12 CenterZ=0 NormalX=0 NormalY=0 NormalZ=1 AngleXU=0 Radius=2.5
    g3: Circle CenterX=5 CenterY=12 CenterZ=0 NormalX=0 NormalY=0 NormalZ=1 AngleXU=0 Radius=2.5
  constraints (8):
    c: Coincident(g0,g-3)
    c: Coincident(g1,g-4)
    c: Equal(g0,g-3)
    c: Equal(g1,g-4)
    c: Coincident(g2,g0)
    c: Coincident(g3,g1)
    c: Diameter(g2) = 5
    c: Equal(g2,g3)
FEATURE [PartDesign::Pad] Pad001
  BaseFeature = -> Pad
  Direction = (0,0,-1)
  Length = 0.5
  Length2 = 10
  Profile = -> Sketch001
  ReferenceAxis = -> Sketch001 [N_Axis]
  Refine = true
  Suppressed = false
  Type = 0
FEATURE [PartDesign::Body] Body  label="TBoneLinkageTopBody"
  AllowCompound = false
  Group = -> [Binder,Sketch,Pad,Sketch001,Pad001]
  Origin = -> Origin001
  Tip = -> Pad001
FEATURE [App::Part] Part  label="TBoneLinkageTopPart"
  Group = -> [Body]
  Origin = -> Origin
---- part ../Parts/TransferLinkage/TransferLinkageLeft.FCStd = doc fcstd_a7fe9f0c62bb ----
FCSTD DOCUMENT  (FreeCAD 1.0R39285 (Git))
Label: TransferLinkageLeft
License: All rights reserved
LicenseURL: https://en.wikipedia.org/wiki/All_rights_reserved
objects: Sketcher::SketchObject×1, App::Link×1, PartDesign::Pad×1, PartDesign::Body×1, App::Part×1
note: 6 computed .brp shape members not serialized (recipe doc carries the construction recipe); baked Part::Feature solids carry a one-line shape summary decoded from their .brp
EXTERNAL_REF file=../../Models/SteeringAckermannModel.FCStd obj=Spreadsheet

FEATURE [Sketcher::SketchObject] Sketch
  ArcFitTolerance = 1e-06
  AttachmentSupport = -> [XY_Plane001]
  FullyConstrained = true
  MakeInternals = false
  MapMode = 5
  expr: Constraints[4] = <<SteeringAckermannSpreadsheet>>.transferlinkagelength
  sketch-geometry (9):
    g0: Circle CenterX=0 CenterY=0 CenterZ=0 NormalX=0 NormalY=0 NormalZ=1 AngleXU=0 Radius=1.66
    g1: Circle CenterX=-32 CenterY=0 CenterZ=0 NormalX=0 NormalY=0 NormalZ=1 AngleXU=0 Radius=1.66
    g2: ArcOfCircle CenterX=0 CenterY=0 CenterZ=0 NormalX=0 NormalY=0 NormalZ=1 AngleXU=0 Radius=2.5 StartAngle=4.71239 EndAngle=7.85398
    g3: LineSegment StartX=8e-16 StartY=2.5 StartZ=0 EndX=-32 EndY=2.5 EndZ=0
    g4: LineSegment StartX=-5e-16 StartY=-2.5 StartZ=0 EndX=-15.88 EndY=-2.5 EndZ=0
    g5: ArcOfCircle CenterX=-32 CenterY=0 CenterZ=0 NormalX=0 NormalY=0 NormalZ=1 AngleXU=0 Radius=2.5 StartAngle=1.5708 EndAngle=5.01328
    g6: LineSegment StartX=-31.2591 StartY=-2.38768 StartZ=0 EndX=-26.1999 EndY=-0.817746 EndZ=0
    g7: ArcOfCircle CenterX=-25.9035 CenterY=-1.77282 CenterZ=0 NormalX=0 NormalY=0 NormalZ=1 AngleXU=0 Radius=1 StartAngle=1.39871 EndAngle=1.87169
    g8: LineSegment StartX=-25.7323 StartY=-0.787589 StartZ=0 EndX=-15.88 EndY=-2.5 EndZ=0
  constraints (21):
    c: Diameter(g0) = 3.32
    c: Coincident(g0,g-1)
    c: Diameter(g1) = 3.32
    c: PointOnObject(g1,g-1)
    c: DistanceX(g1,g0) = 32
    c: Coincident(g2,g0)
    c: Radius(g2) = 2.5
    c: Coincident(g5,g1)
    c: Tangent(g3,g2) = -1.5708
    c: Tangent(g4,g2) = 1.5708
    c: Tangent(g5,g3) = -1.5708
    c: Radius(g5) = 2.5
    c: Distance(g6,g6) = 5.29715
    c: Tangent(g6,g5) = -1.5708
    c: Radius(g7) = 1
    c: Tangent(g7,g6) = 1.5708
    c: Coincident(g8,g4)
    c: Distance(g8,g8) = 10
    c: Tangent(g8,g7) = 1.5708
    c: Parallel(g4,g3)
    c: DistanceX(g4,g4) = 15.88
FEATURE [App::Link] Link  label="SteeringAckermannSpreadsheet"
  LinkedObject = -> <external ../../Models/SteeringAckermannModel.FCStd>#Spreadsheet
FEATURE [PartDesign::Pad] Pad
  Direction = (0,0,1)
  Length = 2
  Length2 = 10
  Profile = -> Sketch
  ReferenceAxis = -> Sketch [N_Axis]
  Refine = true
  Suppressed = false
  Type = 0
FEATURE [PartDesign::Body] Body  label="TransferLinkageLeftBody"
  AllowCompound = false
  Group = -> [Sketch,Pad]
  Origin = -> Origin001
  Tip = -> Pad
FEATURE [App::Part] Part  label="TransferLinkageLeftPart"
  Group = -> [Body]
  Origin = -> Origin
---- part ../Parts/TransferLinkage/TransferLinkageRight.FCStd = doc fcstd_15382c82bdbc ----
FCSTD DOCUMENT  (FreeCAD 1.0R39285 (Git))
Label: TransferLinkageRight
License: All rights reserved
LicenseURL: https://en.wikipedia.org/wiki/All_rights_reserved
objects: PartDesign::SubShapeBinder×1, Part::Mirroring×1, App::Part×1
note: 2 computed .brp shape members not serialized (recipe doc carries the construction recipe); baked Part::Feature solids carry a one-line shape summary decoded from their .brp
EXTERNAL_REF file=TransferLinkageLeft.FCStd obj=Part

FEATURE [PartDesign::SubShapeBinder] Binder  label="TransferLinkageLeftBody"
  BindCopyOnChange = 0
  BindMode = 0
  ClaimChildren = false
  Context = -> Part [Binder.]
  Fuse = false
  MakeFace = true
  OffsetFill = false
  OffsetIntersection = false
  OffsetJoinType = 0
  OffsetOpenResult = false
  PartialLoad = false
  Refine = true
  Relative = true
  Support = -> [<external TransferLinkageLeft.FCStd>#Part[Body.]]
  _Version = 2
FEATURE [Part::Mirroring] Part__Mirroring  label="TransferLinkageRightBody"
  Base = (0,0,0)
  Normal = (1,0,0)
  Source = -> Binder
FEATURE [App::Part] Part  label="TransferLinkageRightPart"
  Group = -> [Binder,Part__Mirroring]
  Origin = -> Origin
---- part ../Parts/Wheel.FCStd = doc fcstd_22f719742fde ----
FCSTD DOCUMENT  (FreeCAD 1.0R39109 (Git))
Label: Wheel
License: All rights reserved
LicenseURL: https://en.wikipedia.org/wiki/All_rights_reserved
objects: Sketcher::SketchObject×5, PartDesign::Pad×4, PartDesign::Pocket×1, PartDesign::Body×1, App::Part×1
note: 26 computed .brp shape members not serialized (recipe doc carries the construction recipe); baked Part::Feature solids carry a one-line shape summary decoded from their .brp

FEATURE [Sketcher::SketchObject] Sketch
  ArcFitTolerance = 1e-06
  AttachmentSupport = -> [YZ_Plane001]
  FullyConstrained = true
  MakeInternals = false
  MapMode = 5
  Placement = pos=(0,0,0) rot=(0.57735,0.57735,0.57735;2.0944rad)
  sketch-geometry (2):
    g0: Circle CenterX=0 CenterY=0 CenterZ=0 NormalX=0 NormalY=0 NormalZ=1 AngleXU=0 Radius=17.5
    g1: Circle CenterX=0 CenterY=0 CenterZ=0 NormalX=0 NormalY=0 NormalZ=1 AngleXU=0 Radius=27.5
  constraints (4):
    c: Diameter(g0) = 35
    c: Coincident(g0,g-1)
    c: Coincident(g1,g0)
    c: Diameter(g1) = 55
FEATURE [PartDesign::Pad] Pad
  Direction = (1,0,0)
  Length = 25
  Length2 = 10
  Placement = pos=(0,0,0) rot=(1,1,1;2.0944rad)
  Profile = -> Sketch
  ReferenceAxis = -> Sketch [N_Axis]
  Refine = true
  Reversed = true
  Suppressed = false
  Type = 0
FEATURE [Sketcher::SketchObject] Sketch001
  ArcFitTolerance = 1e-06
  AttachmentSupport = -> [YZ_Plane001]
  FullyConstrained = true
  MakeInternals = false
  MapMode = 5
  Placement = pos=(0,0,0) rot=(0.57735,0.57735,0.57735;2.0944rad)
  sketch-geometry (9):
    g0: Circle CenterX=0 CenterY=0 CenterZ=0 NormalX=0 NormalY=0 NormalZ=1 AngleXU=0 Radius=17.5
    g1: Circle CenterX=0 CenterY=0 CenterZ=0 NormalX=0 NormalY=0 NormalZ=1 AngleXU=0 Radius=4.55
    g2: LineSegment [constr] StartX=0 StartY=10 StartZ=0 EndX=-8.66025 EndY=-5 EndZ=0
    g3: LineSegment [constr] StartX=-8.66025 StartY=-5 StartZ=0 EndX=8.66025 EndY=-5 EndZ=0
    g4: LineSegment [constr] StartX=8.66025 StartY=-5 StartZ=0 EndX=0 EndY=10 EndZ=0
    g5: Circle [constr] CenterX=0 CenterY=0 CenterZ=0 NormalX=0 NormalY=0 NormalZ=1 AngleXU=0 Radius=10
    g6: Circle CenterX=0 CenterY=10 CenterZ=0 NormalX=0 NormalY=0 NormalZ=1 AngleXU=0 Radius=1.5
    g7: Circle CenterX=-8.66025 CenterY=-5 CenterZ=0 NormalX=0 NormalY=0 NormalZ=1 AngleXU=0 Radius=1.5
    g8: Circle CenterX=8.66025 CenterY=-5 CenterZ=0 NormalX=0 NormalY=0 NormalZ=1 AngleXU=0 Radius=1.5
  constraints (21):
    c: Diameter(g0) = 35
    c: Coincident(g0,g-1)
    c: Diameter(g1) = 9.1
    c: Coincident(g1,g0)
    c: Coincident(g2,g3)
    c: Coincident(g3,g4)
    c: Coincident(g4,g2)
    c: Equal(g2,g3)
    c: Equal(g2,g4)
    c: PointOnObject(g2,g5)
    c: PointOnObject(g3,g5)
    c: PointOnObject(g4,g5)
    c: Coincident(g5,g0)
    c: PointOnObject(g4,g-2)
    c: Diameter(g6) = 3
    c: Coincident(g6,g2)
    c: Diameter(g7) = 3
    c: Coincident(g7,g2)
    c: Diameter(g8) = 3
    c: Coincident(g8,g3)
    c: DistanceY(g0,g2) = 10
FEATURE [PartDesign::Pad] Pad001
  BaseFeature = -> Pad
  Direction = (1,0,0)
  Length = 16
  Length2 = 10
  Placement = pos=(0,0,0) rot=(1,1,1;2.0944rad)
  Profile = -> Sketch001
  ReferenceAxis = -> Sketch001 [N_Axis]
  Refine = true
  Reversed = true
  Suppressed = false
  Type = 0
FEATURE [Sketcher::SketchObject] Sketch002
  ArcFitTolerance = 1e-06
  AttachmentSupport = -> [YZ_Plane001]
  FullyConstrained = true
  MakeInternals = false
  MapMode = 5
  Placement = pos=(0,0,0) rot=(0.57735,0.57735,0.57735;2.0944rad)
  sketch-geometry (1):
    g0: Circle CenterX=0 CenterY=0 CenterZ=0 NormalX=0 NormalY=0 NormalZ=1 AngleXU=0 Radius=17.5
  constraints (2):
    c: Diameter(g0) = 35
    c: Coincident(g0,g-1)
FEATURE [PartDesign::Pocket] Pocket
  BaseFeature = -> Pad001
  Direction = (-1,0,0)
  Length = 13
  Length2 = 5
  Placement = pos=(0,0,0) rot=(1,1,1;2.0944rad)
  Profile = -> Sketch002
  ReferenceAxis = -> Sketch002 [N_Axis]
  Refine = true
  Suppressed = false
  Type = 0
FEATURE [Sketcher::SketchObject] Sketch003
  ArcFitTolerance = 1e-06
  AttachmentSupport = -> [Pocket]
  FullyConstrained = true
  MakeInternals = false
  MapMode = 5
  Placement = pos=(-13,2.9e-15,-1.4e-15) rot=(0.57735,0.57735,0.57735;2.0944rad)
  sketch-geometry (2):
    g0: Circle CenterX=0 CenterY=0 CenterZ=0 NormalX=0 NormalY=0 NormalZ=1 AngleXU=0 Radius=4.55
    g1: Circle CenterX=0 CenterY=0 CenterZ=0 NormalX=0 NormalY=0 NormalZ=1 AngleXU=0 Radius=5.55
  constraints (4):
    c: Diameter(g0) = 9.1
    c: Coincident(g0,g-1)
    c: Coincident(g1,g0)
    c: Diameter(g1) = 11.1
FEATURE [PartDesign::Pad] Pad002
  BaseFeature = -> Pocket
  Direction = (1,0,0)
  Length = 2
  Length2 = 10
  Placement = pos=(0,0,0) rot=(1,1,1;2.0944rad)
  Profile = -> Sketch003
  ReferenceAxis = -> Sketch003 [N_Axis]
  Refine = true
  Suppressed = false
  Type = 0
FEATURE [Sketcher::SketchObject] Sketch004
  ArcFitTolerance = 1e-06
  AttachmentSupport = -> [Pad002]
  FullyConstrained = true
  MakeInternals = false
  MapMode = 5
  Placement = pos=(-16,1.07e-14,-5.3e-15) rot=(0.57735,0.57735,-0.57735;4.18879rad)
  sketch-geometry (2):
    g0: Circle CenterX=0 CenterY=0 CenterZ=0 NormalX=0 NormalY=0 NormalZ=1 AngleXU=0 Radius=4.55
    g1: Circle CenterX=0 CenterY=0 CenterZ=0 NormalX=0 NormalY=0 NormalZ=1 AngleXU=0 Radius=5.55
  constraints (4):
    c: Diameter(g0) = 9.1
    c: Coincident(g0,g-1)
    c: Diameter(g1) = 11.1
    c: Coincident(g1,g0)
FEATURE [PartDesign::Pad] Pad003
  BaseFeature = -> Pad002
  Direction = (-1,0,0)
  Length = 2
  Length2 = 10
  Placement = pos=(0,0,0) rot=(1,1,1;2.0944rad)
  Profile = -> Sketch004
  ReferenceAxis = -> Sketch004 [N_Axis]
  Refine = true
  Suppressed = false
  Type = 0
FEATURE [PartDesign::Body] Body  label="WheelBody"
  AllowCompound = false
  Group = -> [Sketch,Pad,Sketch001,Pad001,Sketch002,Pocket,Sketch003,Pad002,Sketch004,Pad003]
  Origin = -> Origin001
  Tip = -> Pad003
FEATURE [App::Part] Part  label="WheelPart"
  Group = -> [Body]
  Origin = -> Origin
---- part ../Parts/WheelLinkage/WheelLinkageBottomLeft.FCStd = doc fcstd_a23c7c7aa2b5 ----
FCSTD DOCUMENT  (FreeCAD 1.0R39285 (Git))
Label: WheelLinkageBottomLeft
License: All rights reserved
LicenseURL: https://en.wikipedia.org/wiki/All_rights_reserved
objects: Sketcher::SketchObject×4, PartDesign::Pad×4, App::Link×1, PartDesign::Body×1, App::Part×1
note: 21 computed .brp shape members not serialized (recipe doc carries the construction recipe); baked Part::Feature solids carry a one-line shape summary decoded from their .brp
EXTERNAL_REF file=../../Models/SteeringAckermannModel.FCStd obj=Spreadsheet

FEATURE [App::Link] Link  label="SteeringAckermannSpreadsheet"
  LinkedObject = -> <external ../../Models/SteeringAckermannModel.FCStd>#Spreadsheet
FEATURE [Sketcher::SketchObject] Sketch
  ArcFitTolerance = 1e-06
  AttachmentSupport = -> [XY_Plane001]
  FullyConstrained = true
  MakeInternals = false
  MapMode = 5
  expr: Constraints[1] = <<SteeringAckermannSpreadsheet>>.wheellinkagelength
  expr: Constraints[2] = <<SteeringAckermannSpreadsheet>>.wheellinkageangle
  sketch-geometry (9):
    g0: LineSegment [constr] StartX=0 StartY=0 StartZ=0 EndX=-2.70757 EndY=-11.6906 EndZ=0
    g1: ArcOfCircle CenterX=0 CenterY=0 CenterZ=0 NormalX=0 NormalY=0 NormalZ=1 AngleXU=0 Radius=4 StartAngle=5.97216 EndAngle=7.85398
    g2: ArcOfCircle CenterX=-2.70757 CenterY=-11.6906 CenterZ=0 NormalX=0 NormalY=0 NormalZ=1 AngleXU=0 Radius=3 StartAngle=3.3952 EndAngle=5.97216
    g3: LineSegment StartX=3.80809 StartY=-1.22412 StartZ=0 EndX=0.14849 EndY=-12.6086 EndZ=0
    g4: LineSegment StartX=-5.61162 StartY=-12.4432 StartZ=0 EndX=-7.8 EndY=-4 EndZ=0
    g5: LineSegment StartX=-7.8 StartY=-4 StartZ=0 EndX=-7.8 EndY=4 EndZ=0
    g6: LineSegment StartX=-7.8 StartY=4 StartZ=0 EndX=9e-16 EndY=4 EndZ=0
    g7: LineSegment [constr] StartX=0 StartY=0 StartZ=0 EndX=-5 EndY=0 EndZ=0
    g8: Circle CenterX=0 CenterY=0 CenterZ=0 NormalX=0 NormalY=0 NormalZ=1 AngleXU=0 Radius=1.62
  constraints (22):
    c: Coincident(g0,g-1)
    c: Distance(g0,g0) = 12
    c: Angle(g-1,g0) = 1.34321
    c: Coincident(g1,g0)
    c: Coincident(g2,g0)
    c: Coincident(g5,g4)
    c: Vertical(g5)
    c: Coincident(g6,g5)
    c: Tangent(g3,g1) = 1.5708
    c: Tangent(g3,g2) = 1.5708
    c: Tangent(g4,g2) = 1.5708
    c: Tangent(g6,g1) = 1.5708
    c: Horizontal(g6)
    c: Radius(g1) = 4
    c: Radius(g2) = 3
    c: DistanceY(g5,g5) = 8
    c: Coincident(g7,g0)
    c: PointOnObject(g7,g-1)
    c: DistanceX(g7,g7) = 5
    c: Distance(g7,g5) = 2.8
    c: Diameter(g8) = 3.24
    c: Coincident(g8,g0)
FEATURE [PartDesign::Pad] Pad
  Direction = (0,0,1)
  Length = 2
  Length2 = 10
  Profile = -> Sketch
  ReferenceAxis = -> Sketch [N_Axis]
  Refine = true
  Suppressed = false
  Type = 0
FEATURE [Sketcher::SketchObject] Sketch001
  ArcFitTolerance = 1e-06
  AttachmentSupport = -> [Pad]
  ExternalGeometry = -> [Sketch]
  FullyConstrained = true
  MakeInternals = false
  MapMode = 5
  Placement = pos=(0,0,2) rot=(0,0,1;0rad)
  sketch-geometry (1):
    g0: Circle CenterX=-2.70757 CenterY=-11.6906 CenterZ=0 NormalX=0 NormalY=0 NormalZ=1 AngleXU=0 Radius=2.5
  constraints (2):
    c: Coincident(g0,g-3)
    c: Diameter(g0) = 5
FEATURE [PartDesign::Pad] Pad001
  BaseFeature = -> Pad
  Direction = (0,0,1)
  Length = 0.5
  Length2 = 10
  Profile = -> Sketch001
  ReferenceAxis = -> Sketch001 [N_Axis]
  Refine = true
  Suppressed = false
  Type = 0
FEATURE [Sketcher::SketchObject] Sketch002
  ArcFitTolerance = 1e-06
  AttachmentSupport = -> [Pad001]
  ExternalGeometry = -> [Sketch001]
  FullyConstrained = true
  MakeInternals = false
  MapMode = 5
  Placement = pos=(0,0,2.5) rot=(0,0,1;0rad)
  sketch-geometry (1):
    g0: Circle CenterX=-2.70757 CenterY=-11.6906 CenterZ=0 NormalX=0 NormalY=0 NormalZ=1 AngleXU=0 Radius=1.5
  constraints (2):
    c: Diameter(g0) = 3
    c: Coincident(g0,g-3)
FEATURE [PartDesign::Pad] Pad002
  BaseFeature = -> Pad001
  Direction = (0,0,1)
  Length = 4.5
  Length2 = 10
  Profile = -> Sketch002
  ReferenceAxis = -> Sketch002 [N_Axis]
  Refine = true
  Suppressed = false
  Type = 0
FEATURE [Sketcher::SketchObject] Sketch003
  ArcFitTolerance = 1e-06
  AttachmentSupport = -> [Pad002]
  ExternalGeometry = -> [Sketch]
  FullyConstrained = true
  MakeInternals = false
  MapMode = 5
  Placement = pos=(0,0,2) rot=(0,0,1;0rad)
  sketch-geometry (2):
    g0: LineSegment [constr] StartX=0 StartY=0 StartZ=0 EndX=-5 EndY=0 EndZ=0
    g1: Circle CenterX=-5 CenterY=0 CenterZ=0 NormalX=0 NormalY=0 NormalZ=1 AngleXU=0 Radius=1.5
  constraints (5):
    c: Coincident(g0,g-1)
    c: PointOnObject(g0,g-1)
    c: DistanceX(g0,g0) = 5
    c: Diameter(g1) = 3
    c: Coincident(g1,g0)
FEATURE [PartDesign::Pad] Pad003
  BaseFeature = -> Pad002
  Direction = (0,0,1)
  Length = 5
  Length2 = 10
  Profile = -> Sketch003
  ReferenceAxis = -> Sketch003 [N_Axis]
  Refine = true
  Suppressed = false
  Type = 0
FEATURE [PartDesign::Body] Body  label="WheelLinkageBottomBody"
  AllowCompound = false
  Group = -> [Sketch,Pad,Sketch001,Pad001,Sketch002,Pad002,Sketch003,Pad003]
  Origin = -> Origin001
  Tip = -> Pad003
FEATURE [App::Part] Part  label="WheelLinkageBottomLeftPart"
  Group = -> [Body]
  Origin = -> Origin
---- part ../Parts/WheelLinkage/WheelLinkageBottomRight.FCStd = doc fcstd_f47131f818aa ----
FCSTD DOCUMENT  (FreeCAD 1.0R39285 (Git))
Label: WheelLinkageBottomRight
License: All rights reserved
LicenseURL: https://en.wikipedia.org/wiki/All_rights_reserved
objects: PartDesign::SubShapeBinder×1, Part::Mirroring×1, App::Part×1
note: 2 computed .brp shape members not serialized (recipe doc carries the construction recipe); baked Part::Feature solids carry a one-line shape summary decoded from their .brp
EXTERNAL_REF file=WheelLinkageBottomLeft.FCStd obj=Part

FEATURE [PartDesign::SubShapeBinder] Binder  label="WheelLinkageBottomLeftBody"
  BindCopyOnChange = 0
  BindMode = 0
  ClaimChildren = false
  Context = -> Part [Binder.]
  Fuse = false
  MakeFace = true
  OffsetFill = false
  OffsetIntersection = false
  OffsetJoinType = 0
  OffsetOpenResult = false
  PartialLoad = false
  Refine = true
  Relative = true
  Support = -> [<external WheelLinkageBottomLeft.FCStd>#Part[Body.]]
  _Version = 2
FEATURE [Part::Mirroring] Part__Mirroring  label="WheelLinkageBottomRightBody"
  Base = (0,0,0)
  Normal = (1,0,0)
  Source = -> Binder
FEATURE [App::Part] Part  label="WheelLinkageBottomRightPart"
  Group = -> [Binder,Part__Mirroring]
  Origin = -> Origin
---- part ../Parts/WheelLinkage/WheelLinkageTopLeft.FCStd = doc fcstd_06cff2b00e0b ----
FCSTD DOCUMENT  (FreeCAD 1.0R39285 (Git))
Label: WheelLinkageTopLeft
License: All rights reserved
LicenseURL: https://en.wikipedia.org/wiki/All_rights_reserved
objects: PartDesign::SubShapeBinder×3, Sketcher::SketchObject×3, PartDesign::Pad×2, PartDesign::Pocket×2, PartDesign::Body×1, App::Part×1
note: 22 computed .brp shape members not serialized (recipe doc carries the construction recipe); baked Part::Feature solids carry a one-line shape summary decoded from their .brp
EXTERNAL_REF file=WheelLinkageBottomLeft.FCStd obj=Part

FEATURE [PartDesign::SubShapeBinder] Binder  label="WheelLinkageBottomLeftSketch"
  BindCopyOnChange = 0
  BindMode = 0
  ClaimChildren = false
  Context = -> Part [Body.Binder.]
  Fuse = false
  MakeFace = true
  OffsetFill = false
  OffsetIntersection = false
  OffsetJoinType = 0
  OffsetOpenResult = false
  PartialLoad = false
  Refine = true
  Relative = true
  Support = -> [<external WheelLinkageBottomLeft.FCStd>#Part[Body.Sketch.]]
  _Version = 2
FEATURE [PartDesign::Pad] Pad
  Direction = (0,0,1)
  Length = 2
  Length2 = 10
  Profile = -> Binder
  Refine = true
  Reversed = true
  Suppressed = false
  Type = 0
FEATURE [PartDesign::SubShapeBinder] Binder001  label="WheelLinkageBottomLeftSketch003"
  BindCopyOnChange = 0
  BindMode = 0
  ClaimChildren = false
  Context = -> Part [Body.Binder001.]
  Fuse = false
  MakeFace = true
  OffsetFill = false
  OffsetIntersection = false
  OffsetJoinType = 0
  OffsetOpenResult = false
  PartialLoad = false
  Refine = true
  Relative = true
  Support = -> [<external WheelLinkageBottomLeft.FCStd>#Part[Body.Sketch003.]]
  _Version = 2
FEATURE [Sketcher::SketchObject] Sketch
  ArcFitTolerance = 1e-06
  AttachmentSupport = -> [Pad]
  ExternalGeometry = -> [Binder001]
  FullyConstrained = true
  MakeInternals = false
  MapMode = 5
  Placement = pos=(0,0,-2) rot=(1,0,0;3.14159rad)
  sketch-geometry (1):
    g0: Circle CenterX=-5 CenterY=0 CenterZ=0 NormalX=0 NormalY=0 NormalZ=1 AngleXU=0 Radius=1.68
  constraints (2):
    c: Coincident(g0,g-3)
    c: Diameter(g0) = 3.36
FEATURE [PartDesign::Pocket] Pocket
  BaseFeature = -> Pad
  Direction = (0,0,1)
  Length = 0
  Length2 = 5
  Profile = -> Sketch
  ReferenceAxis = -> Sketch [N_Axis]
  Refine = true
  Suppressed = false
  Type = 3
  UpToFace = -> Pad [Face8]
FEATURE [PartDesign::SubShapeBinder] Binder002  label="WheelLinkageBottomLeftSketch002"
  BindCopyOnChange = 0
  BindMode = 0
  ClaimChildren = false
  Context = -> Part [Body.Binder002.]
  Fuse = false
  MakeFace = true
  OffsetFill = false
  OffsetIntersection = false
  OffsetJoinType = 0
  OffsetOpenResult = false
  PartialLoad = false
  Refine = true
  Relative = true
  Support = -> [<external WheelLinkageBottomLeft.FCStd>#Part[Body.Sketch001.]]
  _Version = 2
FEATURE [Sketcher::SketchObject] Sketch001
  ArcFitTolerance = 1e-06
  AttachmentSupport = -> [Pocket]
  ExternalGeometry = -> [Binder002]
  FullyConstrained = true
  MakeInternals = false
  MapMode = 5
  Placement = pos=(0,0,-2) rot=(1,0,0;3.14159rad)
  sketch-geometry (1):
    g0: Circle CenterX=-2.70757 CenterY=11.6906 CenterZ=0 NormalX=0 NormalY=0 NormalZ=1 AngleXU=0 Radius=2.5
  constraints (2):
    c: Coincident(g0,g-3)
    c: Equal(g0,g-3)
FEATURE [PartDesign::Pad] Pad001
  BaseFeature = -> Pocket
  Direction = (0,0,-1)
  Length = 0.5
  Length2 = 10
  Profile = -> Sketch001
  ReferenceAxis = -> Sketch001 [N_Axis]
  Refine = true
  Suppressed = false
  Type = 0
FEATURE [Sketcher::SketchObject] Sketch002
  ArcFitTolerance = 1e-06
  AttachmentSupport = -> [Pad001]
  ExternalGeometry = -> [Sketch001]
  FullyConstrained = true
  MakeInternals = false
  MapMode = 5
  Placement = pos=(0,0,-2.5) rot=(1,0,0;3.14159rad)
  sketch-geometry (1):
    g0: Circle CenterX=-2.70757 CenterY=11.6906 CenterZ=0 NormalX=0 NormalY=0 NormalZ=1 AngleXU=0 Radius=1.64
  constraints (2):
    c: Diameter(g0) = 3.28
    c: Coincident(g0,g-3)
FEATURE [PartDesign::Pocket] Pocket001
  BaseFeature = -> Pad001
  Direction = (0,0,1)
  Length = 0
  Length2 = 5
  Profile = -> Sketch002
  ReferenceAxis = -> Sketch002 [N_Axis]
  Refine = true
  Suppressed = false
  Type = 3
  UpToFace = -> Pad001 [Face4]
FEATURE [PartDesign::Body] Body  label="WheelLinkageTopLeftBody"
  AllowCompound = false
  Group = -> [Binder,Pad,Binder001,Sketch,Pocket,Binder002,Sketch001,Pad001,Sketch002,Pocket001]
  Origin = -> Origin001
  Tip = -> Pocket001
FEATURE [App::Part] Part  label="WheelLinkageTopLeftPart"
  Group = -> [Body]
  Origin = -> Origin
---- part ../Parts/WheelLinkage/WheelLinkageTopRight.FCStd = doc fcstd_321a71ae4978 ----
FCSTD DOCUMENT  (FreeCAD 1.0R39285 (Git))
Label: WheelLinkageTopRight
License: All rights reserved
LicenseURL: https://en.wikipedia.org/wiki/All_rights_reserved
objects: PartDesign::SubShapeBinder×1, Part::Mirroring×1, App::Part×1
note: 2 computed .brp shape members not serialized (recipe doc carries the construction recipe); baked Part::Feature solids carry a one-line shape summary decoded from their .brp
EXTERNAL_REF file=WheelLinkageTopLeft.FCStd obj=Part

FEATURE [PartDesign::SubShapeBinder] Binder  label="WheelLinkageTopLeftBody"
  BindCopyOnChange = 0
  BindMode = 0
  ClaimChildren = false
  Context = -> Part [Binder.]
  Fuse = false
  MakeFace = true
  OffsetFill = false
  OffsetIntersection = false
  OffsetJoinType = 0
  OffsetOpenResult = false
  PartialLoad = false
  Refine = true
  Relative = true
  Support = -> [<external WheelLinkageTopLeft.FCStd>#Part[Body.]]
  _Version = 2
FEATURE [Part::Mirroring] Part__Mirroring  label="WheelLinkageTopRightBody"
  Base = (0,0,0)
  Normal = (1,0,0)
  Source = -> Binder
FEATURE [App::Part] Part  label="WheelLinkageTopRightPart"
  Group = -> [Binder,Part__Mirroring]
  Origin = -> Origin
